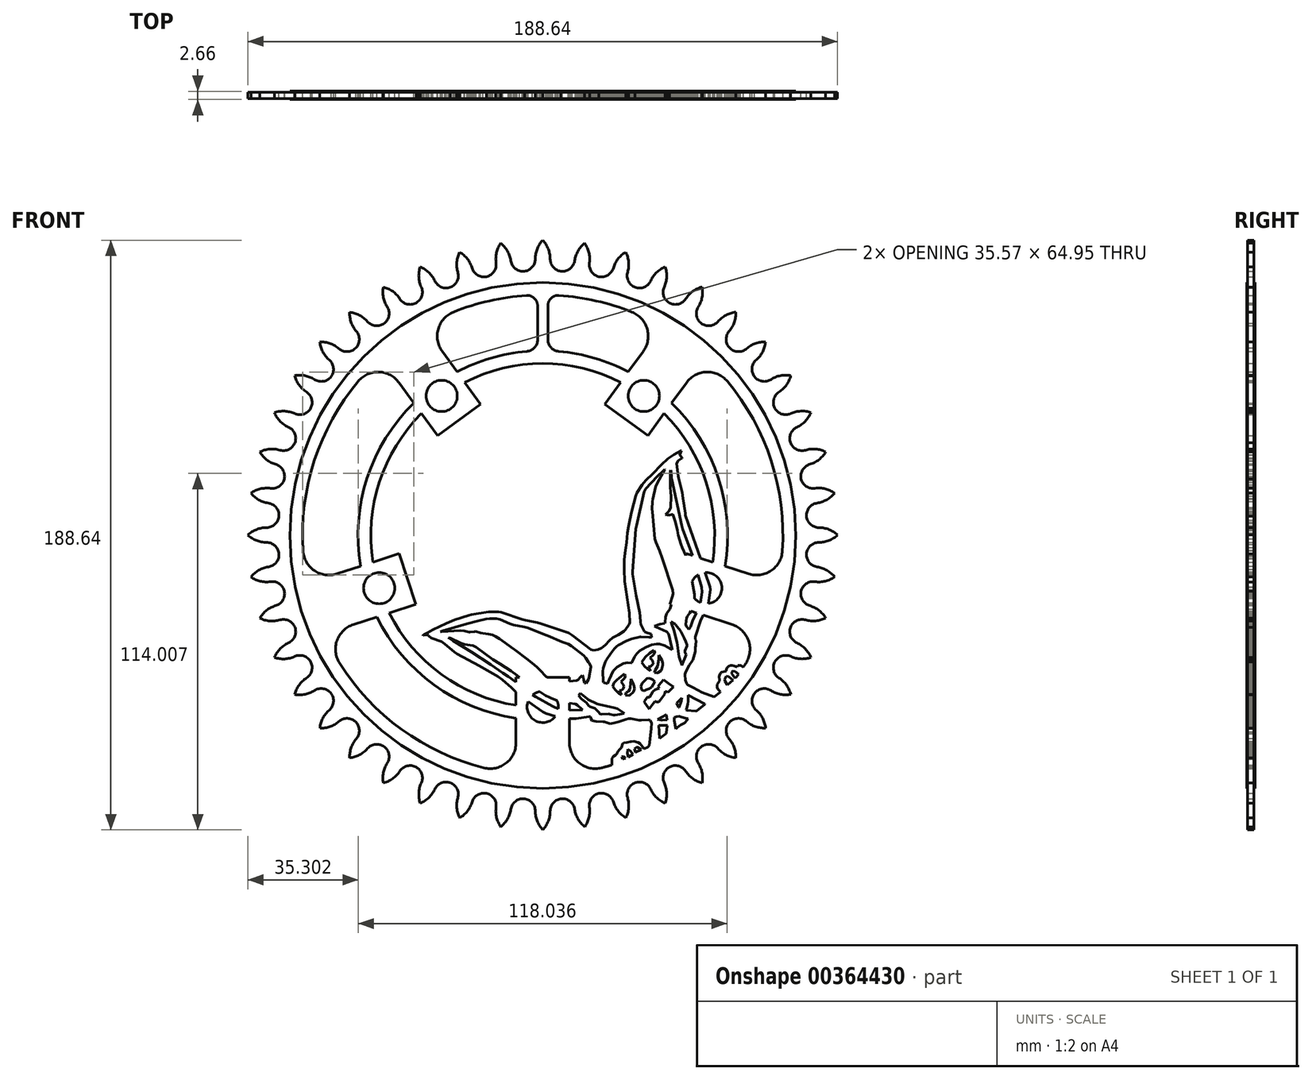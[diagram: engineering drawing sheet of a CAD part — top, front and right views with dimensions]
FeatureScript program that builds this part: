
annotation { "Feature Type Name" : "Feature", "Feature Type Description" : "" }
export const myFeature = defineFeature(function(context is Context, id is Id, definition is map)
    precondition{}
    {
        {
            var Q0;
            Q0=qCreatedBy(makeId("Front.planeOp"),FACE);
            var sketch = newSketch(context, id + "F0", { "sketchPlane" : qUnion([Q0])});
            skArc(sketch, "E0", {"start": v(-6.35, 84.36) * mm, "mid": v(-3.54, 85.52) * mm, "end": v(-2.38, 88.33) * mm});
            skArc(sketch, "E1.MirrorC", {"start": v(6.35, 84.36) * mm, "mid": v(3.54, 85.53) * mm, "end": v(2.38, 88.33) * mm});
            skPoint(sketch, "E2.orphan", {"position": v(12.57, 87.43) * mm});
            skPoint(sketch, "E3.trimOffspring.end.orphan", {"position": v(-12.57, 87.43) * mm});
            skLineSegment(sketch, "E4.trimOffspring", {"start": v(-5.78, 84.4) * mm, "end": v(-5.79, 84.4) * mm});
            skLineSegment(sketch, "E5.trimOffspring", {"start": v(5.78, 84.4) * mm, "end": v(5.79, 84.4) * mm});
            skPoint(sketch, "E6.MirrorCS.start.orphan", {"position": v(6.35, 0) * mm});
            skPoint(sketch, "E7.start.orphan", {"position": v(-6.35, 0) * mm});
            skArc(sketch, "E8.trimOffspring", {"start": v(-2.38, 88.33) * mm, "mid": v(-1.77, 91.55) * mm, "end": v(-0.01, 94.32) * mm});
            skPoint(sketch, "E9.trimOffspring.end.orphan", {"position": v(0, 88.33) * mm});
            skArc(sketch, "E10.trimOffspring", {"start": v(2.38, 88.33) * mm, "mid": v(1.76, 91.56) * mm, "end": v(-0.01, 94.32) * mm});
            skArc(sketch, "E11.1.0", {"start": v(-10.21, 87.77) * mm, "mid": v(-11.3, 90.88) * mm, "end": v(-13.44, 93.36) * mm});
            skPoint(sketch, "E11.1.2", {"position": v(-18.86, 86.53) * mm});
            skPoint(sketch, "E11.1.3", {"position": v(-6.29, 88.34) * mm});
            skArc(sketch, "E11.1.4", {"start": v(-14.93, 87.1) * mm, "mid": v(-14.78, 90.37) * mm, "end": v(-13.44, 93.36) * mm});
            skArc(sketch, "E11.1.5", {"start": v(-5.72, 84.4) * mm, "mid": v(-8.67, 85.16) * mm, "end": v(-10.21, 87.77) * mm});
            skArc(sketch, "E11.1.6", {"start": v(-18.3, 82.6) * mm, "mid": v(-15.68, 84.15) * mm, "end": v(-14.93, 87.1) * mm});
            skArc(sketch, "E11.2.0", {"start": v(-22.6, 85.43) * mm, "mid": v(-24.1, 88.34) * mm, "end": v(-26.59, 90.5) * mm});
            skPoint(sketch, "E11.2.1", {"position": v(-24.88, 84.75) * mm});
            skPoint(sketch, "E11.2.2", {"position": v(-30.98, 82.96) * mm});
            skPoint(sketch, "E11.2.3", {"position": v(-18.8, 86.54) * mm});
            skArc(sketch, "E11.2.4", {"start": v(-27.17, 84.08) * mm, "mid": v(-27.5, 87.35) * mm, "end": v(-26.59, 90.5) * mm});
            skArc(sketch, "E11.2.5", {"start": v(-17.67, 82.73) * mm, "mid": v(-20.7, 83.06) * mm, "end": v(-22.6, 85.43) * mm});
            skArc(sketch, "E11.2.6", {"start": v(-29.86, 79.16) * mm, "mid": v(-27.5, 81.06) * mm, "end": v(-27.17, 84.08) * mm});
            skArc(sketch, "E11.3.0", {"start": v(-34.53, 81.34) * mm, "mid": v(-36.43, 84.01) * mm, "end": v(-39.2, 85.8) * mm});
            skPoint(sketch, "E11.3.1", {"position": v(-36.7, 80.35) * mm});
            skPoint(sketch, "E11.3.2", {"position": v(-42.47, 77.71) * mm});
            skPoint(sketch, "E11.3.3", {"position": v(-30.92, 82.99) * mm});
            skArc(sketch, "E11.3.4", {"start": v(-38.86, 79.36) * mm, "mid": v(-39.64, 82.54) * mm, "end": v(-39.2, 85.8) * mm});
            skArc(sketch, "E11.3.5", {"start": v(-29.27, 79.38) * mm, "mid": v(-32.3, 79.27) * mm, "end": v(-34.53, 81.34) * mm});
            skArc(sketch, "E11.3.6", {"start": v(-40.82, 74.1) * mm, "mid": v(-38.75, 76.32) * mm, "end": v(-38.86, 79.36) * mm});
            skArc(sketch, "E11.4.0", {"start": v(-45.75, 75.6) * mm, "mid": v(-48.02, 77.97) * mm, "end": v(-51, 79.34) * mm});
            skPoint(sketch, "E11.4.1", {"position": v(-47.75, 74.3) * mm});
            skPoint(sketch, "E11.4.2", {"position": v(-53.1, 70.88) * mm});
            skPoint(sketch, "E11.4.3", {"position": v(-42.41, 77.74) * mm});
            skArc(sketch, "E11.4.4", {"start": v(-49.76, 73.02) * mm, "mid": v(-50.98, 76.06) * mm, "end": v(-51, 79.34) * mm});
            skArc(sketch, "E11.4.5", {"start": v(-40.27, 74.4) * mm, "mid": v(-43.26, 73.86) * mm, "end": v(-45.75, 75.6) * mm});
            skArc(sketch, "E11.4.6", {"start": v(-50.95, 67.54) * mm, "mid": v(-49.22, 70.03) * mm, "end": v(-49.76, 73.02) * mm});
            skArc(sketch, "E11.5.0", {"start": v(-56.05, 68.32) * mm, "mid": v(-58.63, 70.35) * mm, "end": v(-61.78, 71.28) * mm});
            skPoint(sketch, "E11.5.1", {"position": v(-57.84, 66.76) * mm});
            skPoint(sketch, "E11.5.2", {"position": v(-62.64, 62.6) * mm});
            skPoint(sketch, "E11.5.3", {"position": v(-53.04, 70.91) * mm});
            skArc(sketch, "E11.5.4", {"start": v(-59.64, 65.2) * mm, "mid": v(-61.29, 68.03) * mm, "end": v(-61.78, 71.28) * mm});
            skArc(sketch, "E11.5.5", {"start": v(-50.44, 67.92) * mm, "mid": v(-53.33, 66.96) * mm, "end": v(-56.05, 68.32) * mm});
            skArc(sketch, "E11.5.6", {"start": v(-60.04, 59.6) * mm, "mid": v(-58.68, 62.32) * mm, "end": v(-59.64, 65.2) * mm});
            skArc(sketch, "E11.6.0", {"start": v(-65.2, 59.65) * mm, "mid": v(-68.04, 61.29) * mm, "end": v(-71.3, 61.76) * mm});
            skPoint(sketch, "E11.6.1", {"position": v(-66.75, 57.85) * mm});
            skPoint(sketch, "E11.6.2", {"position": v(-70.91, 53.05) * mm});
            skPoint(sketch, "E11.6.3", {"position": v(-62.6, 62.64) * mm});
            skArc(sketch, "E11.6.4", {"start": v(-68.31, 56.05) * mm, "mid": v(-70.35, 58.62) * mm, "end": v(-71.3, 61.76) * mm});
            skArc(sketch, "E11.6.5", {"start": v(-59.6, 60.05) * mm, "mid": v(-62.31, 58.69) * mm, "end": v(-65.2, 59.65) * mm});
            skArc(sketch, "E11.6.6", {"start": v(-67.91, 50.45) * mm, "mid": v(-66.95, 53.33) * mm, "end": v(-68.31, 56.05) * mm});
            skArc(sketch, "E11.7.0", {"start": v(-73.02, 49.76) * mm, "mid": v(-76.07, 50.98) * mm, "end": v(-79.35, 50.99) * mm});
            skPoint(sketch, "E11.7.1", {"position": v(-74.3, 47.76) * mm});
            skPoint(sketch, "E11.7.2", {"position": v(-77.74, 42.42) * mm});
            skPoint(sketch, "E11.7.3", {"position": v(-70.87, 53.1) * mm});
            skArc(sketch, "E11.7.4", {"start": v(-75.6, 45.75) * mm, "mid": v(-77.97, 48.01) * mm, "end": v(-79.35, 50.99) * mm});
            skArc(sketch, "E11.7.5", {"start": v(-67.53, 50.95) * mm, "mid": v(-70.03, 49.22) * mm, "end": v(-73.02, 49.76) * mm});
            skArc(sketch, "E11.7.6", {"start": v(-74.4, 40.27) * mm, "mid": v(-73.86, 43.26) * mm, "end": v(-75.6, 45.75) * mm});
            skArc(sketch, "E11.8.0", {"start": v(-79.36, 38.86) * mm, "mid": v(-82.55, 39.63) * mm, "end": v(-85.8, 39.17) * mm});
            skPoint(sketch, "E11.8.1", {"position": v(-80.34, 36.7) * mm});
            skPoint(sketch, "E11.8.2", {"position": v(-82.98, 30.92) * mm});
            skPoint(sketch, "E11.8.3", {"position": v(-77.7, 42.47) * mm});
            skArc(sketch, "E11.8.4", {"start": v(-81.33, 34.53) * mm, "mid": v(-84.01, 36.42) * mm, "end": v(-85.8, 39.17) * mm});
            skArc(sketch, "E11.8.5", {"start": v(-74.1, 40.82) * mm, "mid": v(-76.32, 38.75) * mm, "end": v(-79.36, 38.86) * mm});
            skArc(sketch, "E11.8.6", {"start": v(-79.37, 29.27) * mm, "mid": v(-79.26, 32.3) * mm, "end": v(-81.33, 34.53) * mm});
            skArc(sketch, "E11.9.0", {"start": v(-84.08, 27.17) * mm, "mid": v(-87.35, 27.48) * mm, "end": v(-90.5, 26.56) * mm});
            skPoint(sketch, "E11.9.1", {"position": v(-84.75, 24.89) * mm});
            skPoint(sketch, "E11.9.2", {"position": v(-86.54, 18.8) * mm});
            skPoint(sketch, "E11.9.3", {"position": v(-82.96, 30.98) * mm});
            skArc(sketch, "E11.9.4", {"start": v(-85.42, 22.6) * mm, "mid": v(-88.34, 24.1) * mm, "end": v(-90.5, 26.56) * mm});
            skArc(sketch, "E11.9.5", {"start": v(-79.15, 29.86) * mm, "mid": v(-81.06, 27.5) * mm, "end": v(-84.08, 27.17) * mm});
            skArc(sketch, "E11.9.6", {"start": v(-82.73, 17.68) * mm, "mid": v(-83.05, 20.7) * mm, "end": v(-85.42, 22.6) * mm});
            skArc(sketch, "E11.10.0", {"start": v(-87.1, 14.93) * mm, "mid": v(-90.37, 14.77) * mm, "end": v(-93.36, 13.41) * mm});
            skPoint(sketch, "E11.10.1", {"position": v(-87.43, 12.57) * mm});
            skPoint(sketch, "E11.10.2", {"position": v(-88.33, 6.29) * mm});
            skPoint(sketch, "E11.10.3", {"position": v(-86.52, 18.86) * mm});
            skArc(sketch, "E11.10.4", {"start": v(-87.77, 10.22) * mm, "mid": v(-90.87, 11.28) * mm, "end": v(-93.36, 13.41) * mm});
            skArc(sketch, "E11.10.5", {"start": v(-82.6, 18.3) * mm, "mid": v(-84.15, 15.68) * mm, "end": v(-87.1, 14.93) * mm});
            skArc(sketch, "E11.10.6", {"start": v(-84.4, 5.72) * mm, "mid": v(-85.15, 8.67) * mm, "end": v(-87.77, 10.22) * mm});
            skArc(sketch, "E11.11.0", {"start": v(-88.33, 2.38) * mm, "mid": v(-91.55, 1.76) * mm, "end": v(-94.32, 0) * mm});
            skPoint(sketch, "E11.11.1", {"position": v(-88.33, 0) * mm});
            skPoint(sketch, "E11.11.2", {"position": v(-88.33, -6.35) * mm});
            skPoint(sketch, "E11.11.3", {"position": v(-88.33, 6.35) * mm});
            skArc(sketch, "E11.11.4", {"start": v(-88.33, -2.38) * mm, "mid": v(-91.55, -1.77) * mm, "end": v(-94.32, 0) * mm});
            skArc(sketch, "E11.11.5", {"start": v(-84.36, 6.35) * mm, "mid": v(-85.52, 3.55) * mm, "end": v(-88.33, 2.38) * mm});
            skArc(sketch, "E11.11.6", {"start": v(-84.36, -6.35) * mm, "mid": v(-85.52, -3.54) * mm, "end": v(-88.33, -2.38) * mm});
            skArc(sketch, "E11.12.0", {"start": v(-87.77, -10.21) * mm, "mid": v(-90.87, -11.29) * mm, "end": v(-93.36, -13.43) * mm});
            skPoint(sketch, "E11.12.1", {"position": v(-87.43, -12.57) * mm});
            skPoint(sketch, "E11.12.2", {"position": v(-86.52, -18.85) * mm});
            skPoint(sketch, "E11.12.3", {"position": v(-88.33, -6.28) * mm});
            skArc(sketch, "E11.12.4", {"start": v(-87.09, -14.92) * mm, "mid": v(-90.37, -14.78) * mm, "end": v(-93.36, -13.43) * mm});
            skArc(sketch, "E11.12.5", {"start": v(-84.4, -5.72) * mm, "mid": v(-85.16, -8.66) * mm, "end": v(-87.77, -10.21) * mm});
            skArc(sketch, "E11.12.6", {"start": v(-82.6, -18.29) * mm, "mid": v(-84.15, -15.67) * mm, "end": v(-87.09, -14.92) * mm});
            skArc(sketch, "E11.13.0", {"start": v(-85.42, -22.6) * mm, "mid": v(-88.34, -24.1) * mm, "end": v(-90.5, -26.58) * mm});
            skPoint(sketch, "E11.13.1", {"position": v(-84.75, -24.88) * mm});
            skPoint(sketch, "E11.13.2", {"position": v(-82.96, -30.97) * mm});
            skPoint(sketch, "E11.13.3", {"position": v(-86.54, -18.79) * mm});
            skArc(sketch, "E11.13.4", {"start": v(-84.08, -27.16) * mm, "mid": v(-87.34, -27.49) * mm, "end": v(-90.5, -26.58) * mm});
            skArc(sketch, "E11.13.5", {"start": v(-82.73, -17.67) * mm, "mid": v(-83.06, -20.7) * mm, "end": v(-85.42, -22.6) * mm});
            skArc(sketch, "E11.13.6", {"start": v(-79.15, -29.85) * mm, "mid": v(-81.06, -27.49) * mm, "end": v(-84.08, -27.16) * mm});
            skArc(sketch, "E11.14.0", {"start": v(-81.34, -34.52) * mm, "mid": v(-84.01, -36.43) * mm, "end": v(-85.8, -39.2) * mm});
            skPoint(sketch, "E11.14.1", {"position": v(-80.34, -36.69) * mm});
            skPoint(sketch, "E11.14.2", {"position": v(-77.7, -42.46) * mm});
            skPoint(sketch, "E11.14.3", {"position": v(-82.98, -30.91) * mm});
            skArc(sketch, "E11.14.4", {"start": v(-79.36, -38.85) * mm, "mid": v(-82.54, -39.64) * mm, "end": v(-85.8, -39.2) * mm});
            skArc(sketch, "E11.14.5", {"start": v(-79.37, -29.26) * mm, "mid": v(-79.26, -32.3) * mm, "end": v(-81.34, -34.52) * mm});
            skArc(sketch, "E11.14.6", {"start": v(-74.1, -40.82) * mm, "mid": v(-76.32, -38.75) * mm, "end": v(-79.36, -38.85) * mm});
            skArc(sketch, "E11.15.0", {"start": v(-75.6, -45.75) * mm, "mid": v(-77.97, -48.02) * mm, "end": v(-79.34, -51) * mm});
            skPoint(sketch, "E11.15.1", {"position": v(-74.3, -47.75) * mm});
            skPoint(sketch, "E11.15.2", {"position": v(-70.87, -53.1) * mm});
            skPoint(sketch, "E11.15.3", {"position": v(-77.74, -42.4) * mm});
            skArc(sketch, "E11.15.4", {"start": v(-73.02, -49.75) * mm, "mid": v(-76.06, -50.98) * mm, "end": v(-79.34, -51) * mm});
            skArc(sketch, "E11.15.5", {"start": v(-74.4, -40.26) * mm, "mid": v(-73.86, -43.25) * mm, "end": v(-75.6, -45.75) * mm});
            skArc(sketch, "E11.15.6", {"start": v(-67.53, -50.94) * mm, "mid": v(-70.03, -49.21) * mm, "end": v(-73.02, -49.75) * mm});
            skArc(sketch, "E11.16.0", {"start": v(-68.31, -56.04) * mm, "mid": v(-70.34, -58.62) * mm, "end": v(-71.27, -61.77) * mm});
            skPoint(sketch, "E11.16.1", {"position": v(-66.75, -57.84) * mm});
            skPoint(sketch, "E11.16.2", {"position": v(-62.6, -62.64) * mm});
            skPoint(sketch, "E11.16.3", {"position": v(-70.91, -53.04) * mm});
            skArc(sketch, "E11.16.4", {"start": v(-65.2, -59.64) * mm, "mid": v(-68.03, -61.29) * mm, "end": v(-71.27, -61.77) * mm});
            skArc(sketch, "E11.16.5", {"start": v(-67.91, -50.44) * mm, "mid": v(-66.95, -53.32) * mm, "end": v(-68.31, -56.04) * mm});
            skArc(sketch, "E11.16.6", {"start": v(-59.6, -60.04) * mm, "mid": v(-62.31, -58.68) * mm, "end": v(-65.2, -59.64) * mm});
            skArc(sketch, "E11.17.0", {"start": v(-59.64, -65.2) * mm, "mid": v(-61.28, -68.04) * mm, "end": v(-61.76, -71.29) * mm});
            skPoint(sketch, "E11.17.1", {"position": v(-57.84, -66.75) * mm});
            skPoint(sketch, "E11.17.2", {"position": v(-53.04, -70.9) * mm});
            skPoint(sketch, "E11.17.3", {"position": v(-62.64, -62.6) * mm});
            skArc(sketch, "E11.17.4", {"start": v(-56.04, -68.3) * mm, "mid": v(-58.61, -70.34) * mm, "end": v(-61.76, -71.29) * mm});
            skArc(sketch, "E11.17.5", {"start": v(-60.04, -59.6) * mm, "mid": v(-58.68, -62.3) * mm, "end": v(-59.64, -65.2) * mm});
            skArc(sketch, "E11.17.6", {"start": v(-50.44, -67.9) * mm, "mid": v(-53.33, -66.95) * mm, "end": v(-56.04, -68.3) * mm});
            skArc(sketch, "E11.18.0", {"start": v(-49.76, -73.02) * mm, "mid": v(-50.98, -76.07) * mm, "end": v(-50.98, -79.35) * mm});
            skPoint(sketch, "E11.18.1", {"position": v(-47.75, -74.3) * mm});
            skPoint(sketch, "E11.18.2", {"position": v(-42.41, -77.73) * mm});
            skPoint(sketch, "E11.18.3", {"position": v(-53.1, -70.87) * mm});
            skArc(sketch, "E11.18.4", {"start": v(-45.75, -75.59) * mm, "mid": v(-48, -77.97) * mm, "end": v(-50.98, -79.35) * mm});
            skArc(sketch, "E11.18.5", {"start": v(-50.95, -67.53) * mm, "mid": v(-49.22, -70.03) * mm, "end": v(-49.76, -73.02) * mm});
            skArc(sketch, "E11.18.6", {"start": v(-40.27, -74.4) * mm, "mid": v(-43.26, -73.86) * mm, "end": v(-45.75, -75.59) * mm});
            skArc(sketch, "E11.19.0", {"start": v(-38.86, -79.36) * mm, "mid": v(-39.63, -82.55) * mm, "end": v(-39.17, -85.8) * mm});
            skPoint(sketch, "E11.19.1", {"position": v(-36.7, -80.34) * mm});
            skPoint(sketch, "E11.19.2", {"position": v(-30.92, -82.98) * mm});
            skPoint(sketch, "E11.19.3", {"position": v(-42.47, -77.7) * mm});
            skArc(sketch, "E11.19.4", {"start": v(-34.53, -81.33) * mm, "mid": v(-36.42, -84) * mm, "end": v(-39.17, -85.8) * mm});
            skArc(sketch, "E11.19.5", {"start": v(-40.82, -74.1) * mm, "mid": v(-38.75, -76.32) * mm, "end": v(-38.86, -79.36) * mm});
            skArc(sketch, "E11.19.6", {"start": v(-29.27, -79.37) * mm, "mid": v(-32.3, -79.26) * mm, "end": v(-34.53, -81.33) * mm});
            skArc(sketch, "E11.20.0", {"start": v(-27.17, -84.08) * mm, "mid": v(-27.48, -87.35) * mm, "end": v(-26.56, -90.5) * mm});
            skPoint(sketch, "E11.20.1", {"position": v(-24.88, -84.74) * mm});
            skPoint(sketch, "E11.20.2", {"position": v(-18.8, -86.53) * mm});
            skPoint(sketch, "E11.20.3", {"position": v(-30.98, -82.96) * mm});
            skArc(sketch, "E11.20.4", {"start": v(-22.6, -85.42) * mm, "mid": v(-24.1, -88.34) * mm, "end": v(-26.56, -90.5) * mm});
            skArc(sketch, "E11.20.5", {"start": v(-29.86, -79.15) * mm, "mid": v(-27.5, -81.06) * mm, "end": v(-27.17, -84.08) * mm});
            skArc(sketch, "E11.20.6", {"start": v(-17.67, -82.73) * mm, "mid": v(-20.7, -83.05) * mm, "end": v(-22.6, -85.42) * mm});
            skArc(sketch, "E11.21.0", {"start": v(-14.93, -87.09) * mm, "mid": v(-14.77, -90.37) * mm, "end": v(-13.4, -93.36) * mm});
            skPoint(sketch, "E11.21.1", {"position": v(-12.57, -87.42) * mm});
            skPoint(sketch, "E11.21.2", {"position": v(-6.29, -88.33) * mm});
            skPoint(sketch, "E11.21.3", {"position": v(-18.86, -86.52) * mm});
            skArc(sketch, "E11.21.4", {"start": v(-10.21, -87.76) * mm, "mid": v(-11.28, -90.87) * mm, "end": v(-13.4, -93.36) * mm});
            skArc(sketch, "E11.21.5", {"start": v(-18.3, -82.6) * mm, "mid": v(-15.68, -84.14) * mm, "end": v(-14.93, -87.09) * mm});
            skArc(sketch, "E11.21.6", {"start": v(-5.72, -84.4) * mm, "mid": v(-8.66, -85.15) * mm, "end": v(-10.21, -87.76) * mm});
            skArc(sketch, "E11.22.0", {"start": v(-2.38, -88.33) * mm, "mid": v(-1.76, -91.55) * mm, "end": v(0.01, -94.32) * mm});
            skPoint(sketch, "E11.22.1", {"position": v(0, -88.32) * mm});
            skPoint(sketch, "E11.22.2", {"position": v(6.35, -88.32) * mm});
            skPoint(sketch, "E11.22.3", {"position": v(-6.35, -88.32) * mm});
            skArc(sketch, "E11.22.4", {"start": v(2.38, -88.32) * mm, "mid": v(1.77, -91.55) * mm, "end": v(0.01, -94.32) * mm});
            skArc(sketch, "E11.22.5", {"start": v(-6.35, -84.35) * mm, "mid": v(-3.54, -85.52) * mm, "end": v(-2.38, -88.33) * mm});
            skArc(sketch, "E11.22.6", {"start": v(6.35, -84.35) * mm, "mid": v(3.54, -85.52) * mm, "end": v(2.38, -88.32) * mm});
            skArc(sketch, "E11.23.0", {"start": v(10.21, -87.77) * mm, "mid": v(11.3, -90.87) * mm, "end": v(13.44, -93.35) * mm});
            skPoint(sketch, "E11.23.1", {"position": v(12.57, -87.42) * mm});
            skPoint(sketch, "E11.23.2", {"position": v(18.86, -86.52) * mm});
            skPoint(sketch, "E11.23.3", {"position": v(6.29, -88.33) * mm});
            skArc(sketch, "E11.23.4", {"start": v(14.93, -87.08) * mm, "mid": v(14.78, -90.36) * mm, "end": v(13.44, -93.35) * mm});
            skArc(sketch, "E11.23.5", {"start": v(5.72, -84.4) * mm, "mid": v(8.67, -85.15) * mm, "end": v(10.21, -87.77) * mm});
            skArc(sketch, "E11.23.6", {"start": v(18.3, -82.6) * mm, "mid": v(15.68, -84.14) * mm, "end": v(14.93, -87.08) * mm});
            skArc(sketch, "E11.24.0", {"start": v(22.6, -85.42) * mm, "mid": v(24.1, -88.34) * mm, "end": v(26.59, -90.5) * mm});
            skPoint(sketch, "E11.24.1", {"position": v(24.88, -84.74) * mm});
            skPoint(sketch, "E11.24.2", {"position": v(30.98, -82.96) * mm});
            skPoint(sketch, "E11.24.3", {"position": v(18.8, -86.53) * mm});
            skArc(sketch, "E11.24.4", {"start": v(27.17, -84.07) * mm, "mid": v(27.5, -87.34) * mm, "end": v(26.59, -90.5) * mm});
            skArc(sketch, "E11.24.5", {"start": v(17.67, -82.73) * mm, "mid": v(20.7, -83.05) * mm, "end": v(22.6, -85.42) * mm});
            skArc(sketch, "E11.24.6", {"start": v(29.86, -79.15) * mm, "mid": v(27.5, -81.05) * mm, "end": v(27.17, -84.07) * mm});
            skArc(sketch, "E11.25.0", {"start": v(34.53, -81.33) * mm, "mid": v(36.43, -84) * mm, "end": v(39.2, -85.79) * mm});
            skPoint(sketch, "E11.25.1", {"position": v(36.7, -80.34) * mm});
            skPoint(sketch, "E11.25.2", {"position": v(42.47, -77.7) * mm});
            skPoint(sketch, "E11.25.3", {"position": v(30.92, -82.98) * mm});
            skArc(sketch, "E11.25.4", {"start": v(38.86, -79.35) * mm, "mid": v(39.64, -82.54) * mm, "end": v(39.2, -85.79) * mm});
            skArc(sketch, "E11.25.5", {"start": v(29.27, -79.37) * mm, "mid": v(32.3, -79.26) * mm, "end": v(34.53, -81.33) * mm});
            skArc(sketch, "E11.25.6", {"start": v(40.82, -74.1) * mm, "mid": v(38.75, -76.32) * mm, "end": v(38.86, -79.35) * mm});
            skArc(sketch, "E11.26.0", {"start": v(45.75, -75.6) * mm, "mid": v(48.02, -77.97) * mm, "end": v(51, -79.34) * mm});
            skPoint(sketch, "E11.26.1", {"position": v(47.75, -74.3) * mm});
            skPoint(sketch, "E11.26.2", {"position": v(53.1, -70.87) * mm});
            skPoint(sketch, "E11.26.3", {"position": v(42.41, -77.73) * mm});
            skArc(sketch, "E11.26.4", {"start": v(49.76, -73.01) * mm, "mid": v(50.98, -76.06) * mm, "end": v(51, -79.34) * mm});
            skArc(sketch, "E11.26.5", {"start": v(40.27, -74.4) * mm, "mid": v(43.26, -73.86) * mm, "end": v(45.75, -75.6) * mm});
            skArc(sketch, "E11.26.6", {"start": v(50.95, -67.53) * mm, "mid": v(49.22, -70.02) * mm, "end": v(49.76, -73.01) * mm});
            skArc(sketch, "E11.27.0", {"start": v(56.05, -68.31) * mm, "mid": v(58.63, -70.34) * mm, "end": v(61.78, -71.27) * mm});
            skPoint(sketch, "E11.27.1", {"position": v(57.84, -66.75) * mm});
            skPoint(sketch, "E11.27.2", {"position": v(62.64, -62.6) * mm});
            skPoint(sketch, "E11.27.3", {"position": v(53.04, -70.9) * mm});
            skArc(sketch, "E11.27.4", {"start": v(59.64, -65.19) * mm, "mid": v(61.29, -68.03) * mm, "end": v(61.78, -71.27) * mm});
            skArc(sketch, "E11.27.5", {"start": v(50.44, -67.9) * mm, "mid": v(53.33, -66.95) * mm, "end": v(56.05, -68.31) * mm});
            skArc(sketch, "E11.27.6", {"start": v(60.04, -59.6) * mm, "mid": v(58.68, -62.3) * mm, "end": v(59.64, -65.19) * mm});
            skArc(sketch, "E11.28.0", {"start": v(65.2, -59.64) * mm, "mid": v(68.04, -61.28) * mm, "end": v(71.3, -61.75) * mm});
            skPoint(sketch, "E11.28.1", {"position": v(66.75, -57.84) * mm});
            skPoint(sketch, "E11.28.2", {"position": v(70.91, -53.04) * mm});
            skPoint(sketch, "E11.28.3", {"position": v(62.6, -62.64) * mm});
            skArc(sketch, "E11.28.4", {"start": v(68.31, -56.04) * mm, "mid": v(70.35, -58.61) * mm, "end": v(71.3, -61.75) * mm});
            skArc(sketch, "E11.28.5", {"start": v(59.6, -60.04) * mm, "mid": v(62.31, -58.68) * mm, "end": v(65.2, -59.64) * mm});
            skArc(sketch, "E11.28.6", {"start": v(67.91, -50.44) * mm, "mid": v(66.95, -53.32) * mm, "end": v(68.31, -56.04) * mm});
            skArc(sketch, "E11.29.0", {"start": v(73.02, -49.75) * mm, "mid": v(76.07, -50.97) * mm, "end": v(79.35, -50.98) * mm});
            skPoint(sketch, "E11.29.1", {"position": v(74.3, -47.75) * mm});
            skPoint(sketch, "E11.29.2", {"position": v(77.74, -42.4) * mm});
            skPoint(sketch, "E11.29.3", {"position": v(70.87, -53.1) * mm});
            skArc(sketch, "E11.29.4", {"start": v(75.6, -45.75) * mm, "mid": v(77.97, -48) * mm, "end": v(79.35, -50.98) * mm});
            skArc(sketch, "E11.29.5", {"start": v(67.53, -50.94) * mm, "mid": v(70.03, -49.21) * mm, "end": v(73.02, -49.75) * mm});
            skArc(sketch, "E11.29.6", {"start": v(74.4, -40.26) * mm, "mid": v(73.86, -43.25) * mm, "end": v(75.6, -45.75) * mm});
            skArc(sketch, "E11.30.0", {"start": v(79.36, -38.86) * mm, "mid": v(82.55, -39.63) * mm, "end": v(85.8, -39.17) * mm});
            skPoint(sketch, "E11.30.1", {"position": v(80.34, -36.69) * mm});
            skPoint(sketch, "E11.30.2", {"position": v(82.98, -30.91) * mm});
            skPoint(sketch, "E11.30.3", {"position": v(77.7, -42.46) * mm});
            skArc(sketch, "E11.30.4", {"start": v(81.33, -34.52) * mm, "mid": v(84.01, -36.42) * mm, "end": v(85.8, -39.17) * mm});
            skArc(sketch, "E11.30.5", {"start": v(74.1, -40.82) * mm, "mid": v(76.32, -38.74) * mm, "end": v(79.36, -38.86) * mm});
            skArc(sketch, "E11.30.6", {"start": v(79.37, -29.26) * mm, "mid": v(79.26, -32.3) * mm, "end": v(81.33, -34.52) * mm});
            skArc(sketch, "E11.31.0", {"start": v(84.08, -27.17) * mm, "mid": v(87.35, -27.48) * mm, "end": v(90.5, -26.56) * mm});
            skPoint(sketch, "E11.31.1", {"position": v(84.75, -24.88) * mm});
            skPoint(sketch, "E11.31.2", {"position": v(86.54, -18.79) * mm});
            skPoint(sketch, "E11.31.3", {"position": v(82.96, -30.97) * mm});
            skArc(sketch, "E11.31.4", {"start": v(85.42, -22.6) * mm, "mid": v(88.34, -24.1) * mm, "end": v(90.5, -26.56) * mm});
            skArc(sketch, "E11.31.5", {"start": v(79.15, -29.85) * mm, "mid": v(81.06, -27.49) * mm, "end": v(84.08, -27.17) * mm});
            skArc(sketch, "E11.31.6", {"start": v(82.73, -17.67) * mm, "mid": v(83.05, -20.7) * mm, "end": v(85.42, -22.6) * mm});
            skArc(sketch, "E11.32.0", {"start": v(87.1, -14.92) * mm, "mid": v(90.37, -14.76) * mm, "end": v(93.36, -13.4) * mm});
            skPoint(sketch, "E11.32.1", {"position": v(87.43, -12.57) * mm});
            skPoint(sketch, "E11.32.2", {"position": v(88.33, -6.28) * mm});
            skPoint(sketch, "E11.32.3", {"position": v(86.52, -18.85) * mm});
            skArc(sketch, "E11.32.4", {"start": v(87.77, -10.2) * mm, "mid": v(90.87, -11.27) * mm, "end": v(93.36, -13.4) * mm});
            skArc(sketch, "E11.32.5", {"start": v(82.6, -18.29) * mm, "mid": v(84.15, -15.67) * mm, "end": v(87.1, -14.92) * mm});
            skArc(sketch, "E11.32.6", {"start": v(84.4, -5.72) * mm, "mid": v(85.15, -8.66) * mm, "end": v(87.77, -10.2) * mm});
            skArc(sketch, "E11.33.0", {"start": v(88.33, -2.38) * mm, "mid": v(91.55, -1.75) * mm, "end": v(94.32, 0.02) * mm});
            skPoint(sketch, "E11.33.1", {"position": v(88.33, 0) * mm});
            skPoint(sketch, "E11.33.2", {"position": v(88.33, 6.35) * mm});
            skPoint(sketch, "E11.33.3", {"position": v(88.33, -6.35) * mm});
            skArc(sketch, "E11.33.4", {"start": v(88.33, 2.38) * mm, "mid": v(91.55, 1.77) * mm, "end": v(94.32, 0.02) * mm});
            skArc(sketch, "E11.33.5", {"start": v(84.36, -6.35) * mm, "mid": v(85.52, -3.54) * mm, "end": v(88.33, -2.38) * mm});
            skArc(sketch, "E11.33.6", {"start": v(84.36, 6.35) * mm, "mid": v(85.52, 3.55) * mm, "end": v(88.33, 2.38) * mm});
            skArc(sketch, "E11.34.0", {"start": v(87.77, 10.22) * mm, "mid": v(90.87, 11.3) * mm, "end": v(93.36, 13.44) * mm});
            skPoint(sketch, "E11.34.1", {"position": v(87.43, 12.57) * mm});
            skPoint(sketch, "E11.34.2", {"position": v(86.52, 18.86) * mm});
            skPoint(sketch, "E11.34.3", {"position": v(88.33, 6.29) * mm});
            skArc(sketch, "E11.34.4", {"start": v(87.09, 14.93) * mm, "mid": v(90.37, 14.78) * mm, "end": v(93.36, 13.44) * mm});
            skArc(sketch, "E11.34.5", {"start": v(84.4, 5.72) * mm, "mid": v(85.16, 8.67) * mm, "end": v(87.77, 10.22) * mm});
            skArc(sketch, "E11.34.6", {"start": v(82.6, 18.3) * mm, "mid": v(84.15, 15.68) * mm, "end": v(87.09, 14.93) * mm});
            skArc(sketch, "E11.35.0", {"start": v(85.42, 22.6) * mm, "mid": v(88.34, 24.11) * mm, "end": v(90.5, 26.59) * mm});
            skPoint(sketch, "E11.35.1", {"position": v(84.75, 24.89) * mm});
            skPoint(sketch, "E11.35.2", {"position": v(82.96, 30.98) * mm});
            skPoint(sketch, "E11.35.3", {"position": v(86.54, 18.8) * mm});
            skArc(sketch, "E11.35.4", {"start": v(84.08, 27.17) * mm, "mid": v(87.34, 27.5) * mm, "end": v(90.5, 26.59) * mm});
            skArc(sketch, "E11.35.5", {"start": v(82.73, 17.68) * mm, "mid": v(83.06, 20.7) * mm, "end": v(85.42, 22.6) * mm});
            skArc(sketch, "E11.35.6", {"start": v(79.15, 29.86) * mm, "mid": v(81.06, 27.5) * mm, "end": v(84.08, 27.17) * mm});
            skArc(sketch, "E11.36.0", {"start": v(81.34, 34.53) * mm, "mid": v(84.01, 36.44) * mm, "end": v(85.8, 39.2) * mm});
            skPoint(sketch, "E11.36.1", {"position": v(80.34, 36.7) * mm});
            skPoint(sketch, "E11.36.2", {"position": v(77.7, 42.47) * mm});
            skPoint(sketch, "E11.36.3", {"position": v(82.98, 30.92) * mm});
            skArc(sketch, "E11.36.4", {"start": v(79.36, 38.86) * mm, "mid": v(82.54, 39.64) * mm, "end": v(85.8, 39.2) * mm});
            skArc(sketch, "E11.36.5", {"start": v(79.37, 29.27) * mm, "mid": v(79.26, 32.3) * mm, "end": v(81.34, 34.53) * mm});
            skArc(sketch, "E11.36.6", {"start": v(74.1, 40.82) * mm, "mid": v(76.32, 38.75) * mm, "end": v(79.36, 38.86) * mm});
            skArc(sketch, "E11.37.0", {"start": v(75.6, 45.76) * mm, "mid": v(77.97, 48.02) * mm, "end": v(79.34, 51) * mm});
            skPoint(sketch, "E11.37.1", {"position": v(74.3, 47.76) * mm});
            skPoint(sketch, "E11.37.2", {"position": v(70.87, 53.1) * mm});
            skPoint(sketch, "E11.37.3", {"position": v(77.74, 42.42) * mm});
            skArc(sketch, "E11.37.4", {"start": v(73.02, 49.76) * mm, "mid": v(76.06, 50.99) * mm, "end": v(79.34, 51) * mm});
            skArc(sketch, "E11.37.5", {"start": v(74.4, 40.27) * mm, "mid": v(73.86, 43.26) * mm, "end": v(75.6, 45.76) * mm});
            skArc(sketch, "E11.37.6", {"start": v(67.53, 50.95) * mm, "mid": v(70.03, 49.22) * mm, "end": v(73.02, 49.76) * mm});
            skArc(sketch, "E11.38.0", {"start": v(68.31, 56.05) * mm, "mid": v(70.34, 58.63) * mm, "end": v(71.27, 61.78) * mm});
            skPoint(sketch, "E11.38.1", {"position": v(66.75, 57.85) * mm});
            skPoint(sketch, "E11.38.2", {"position": v(62.6, 62.64) * mm});
            skPoint(sketch, "E11.38.3", {"position": v(70.91, 53.05) * mm});
            skArc(sketch, "E11.38.4", {"start": v(65.2, 59.64) * mm, "mid": v(68.03, 61.3) * mm, "end": v(71.27, 61.78) * mm});
            skArc(sketch, "E11.38.5", {"start": v(67.91, 50.45) * mm, "mid": v(66.95, 53.33) * mm, "end": v(68.31, 56.05) * mm});
            skArc(sketch, "E11.38.6", {"start": v(59.6, 60.05) * mm, "mid": v(62.31, 58.69) * mm, "end": v(65.2, 59.64) * mm});
            skArc(sketch, "E11.39.0", {"start": v(59.64, 65.2) * mm, "mid": v(61.28, 68.05) * mm, "end": v(61.76, 71.3) * mm});
            skPoint(sketch, "E11.39.1", {"position": v(57.84, 66.76) * mm});
            skPoint(sketch, "E11.39.2", {"position": v(53.04, 70.91) * mm});
            skPoint(sketch, "E11.39.3", {"position": v(62.64, 62.6) * mm});
            skArc(sketch, "E11.39.4", {"start": v(56.04, 68.32) * mm, "mid": v(58.61, 70.35) * mm, "end": v(61.76, 71.3) * mm});
            skArc(sketch, "E11.39.5", {"start": v(60.04, 59.6) * mm, "mid": v(58.68, 62.32) * mm, "end": v(59.64, 65.2) * mm});
            skArc(sketch, "E11.39.6", {"start": v(50.44, 67.92) * mm, "mid": v(53.33, 66.96) * mm, "end": v(56.04, 68.32) * mm});
            skArc(sketch, "E11.40.0", {"start": v(49.76, 73.03) * mm, "mid": v(50.98, 76.07) * mm, "end": v(50.98, 79.36) * mm});
            skPoint(sketch, "E11.40.1", {"position": v(47.75, 74.3) * mm});
            skPoint(sketch, "E11.40.2", {"position": v(42.41, 77.74) * mm});
            skPoint(sketch, "E11.40.3", {"position": v(53.1, 70.88) * mm});
            skArc(sketch, "E11.40.4", {"start": v(45.75, 75.6) * mm, "mid": v(48, 77.98) * mm, "end": v(50.98, 79.36) * mm});
            skArc(sketch, "E11.40.5", {"start": v(50.95, 67.54) * mm, "mid": v(49.22, 70.03) * mm, "end": v(49.76, 73.03) * mm});
            skArc(sketch, "E11.40.6", {"start": v(40.27, 74.4) * mm, "mid": v(43.26, 73.86) * mm, "end": v(45.75, 75.6) * mm});
            skArc(sketch, "E11.41.0", {"start": v(38.86, 79.36) * mm, "mid": v(39.63, 82.55) * mm, "end": v(39.17, 85.8) * mm});
            skPoint(sketch, "E11.41.1", {"position": v(36.7, 80.35) * mm});
            skPoint(sketch, "E11.41.2", {"position": v(30.92, 82.99) * mm});
            skPoint(sketch, "E11.41.3", {"position": v(42.47, 77.71) * mm});
            skArc(sketch, "E11.41.4", {"start": v(34.53, 81.34) * mm, "mid": v(36.42, 84.02) * mm, "end": v(39.17, 85.8) * mm});
            skArc(sketch, "E11.41.5", {"start": v(40.82, 74.1) * mm, "mid": v(38.75, 76.33) * mm, "end": v(38.86, 79.36) * mm});
            skArc(sketch, "E11.41.6", {"start": v(29.27, 79.38) * mm, "mid": v(32.3, 79.27) * mm, "end": v(34.53, 81.34) * mm});
            skArc(sketch, "E11.42.0", {"start": v(27.17, 84.09) * mm, "mid": v(27.48, 87.35) * mm, "end": v(26.56, 90.5) * mm});
            skPoint(sketch, "E11.42.1", {"position": v(24.88, 84.75) * mm});
            skPoint(sketch, "E11.42.2", {"position": v(18.8, 86.54) * mm});
            skPoint(sketch, "E11.42.3", {"position": v(30.98, 82.96) * mm});
            skArc(sketch, "E11.42.4", {"start": v(22.6, 85.42) * mm, "mid": v(24.1, 88.34) * mm, "end": v(26.56, 90.5) * mm});
            skArc(sketch, "E11.42.5", {"start": v(29.86, 79.16) * mm, "mid": v(27.5, 81.06) * mm, "end": v(27.17, 84.09) * mm});
            skArc(sketch, "E11.42.6", {"start": v(17.67, 82.73) * mm, "mid": v(20.7, 83.06) * mm, "end": v(22.6, 85.42) * mm});
            skArc(sketch, "E11.43.0", {"start": v(14.93, 87.1) * mm, "mid": v(14.77, 90.38) * mm, "end": v(13.4, 93.37) * mm});
            skPoint(sketch, "E11.43.2", {"position": v(6.29, 88.34) * mm});
            skPoint(sketch, "E11.43.3", {"position": v(18.86, 86.53) * mm});
            skArc(sketch, "E11.43.4", {"start": v(10.21, 87.77) * mm, "mid": v(11.28, 90.87) * mm, "end": v(13.4, 93.37) * mm});
            skArc(sketch, "E11.43.5", {"start": v(18.3, 82.6) * mm, "mid": v(15.68, 84.15) * mm, "end": v(14.93, 87.1) * mm});
            skArc(sketch, "E11.43.6", {"start": v(5.72, 84.4) * mm, "mid": v(8.66, 85.16) * mm, "end": v(10.21, 87.77) * mm});
            skPoint(sketch, "E11.center", {"position": v(0, 0) * mm});
            skCircle(sketch, "E12", {"center": v(0, 0) * mm, "radius": 76.83 * mm});
            skCircle(sketch, "E13", {"center": v(0, 0) * mm, "radius": 55 * mm, "construction": true});
            skPoint(sketch, "E14.visualSharp", {"position": v(-8.57, -72.7) * mm});
            skPoint(sketch, "E15.visualSharp", {"position": v(8.57, -72.7) * mm});
            skCircle(sketch, "E16", {"center": v(0, -55) * mm, "radius": 5 * mm});
            skLineSegment(sketch, "E17", {"start": v(-8.54, -45.5) * mm, "end": v(-8.54, -66.46) * mm});
            skArc(sketch, "E18", {"start": v(-18.85, -74.48) * mm, "mid": v(-11.73, -72.99) * mm, "end": v(-8.54, -66.46) * mm});
            skLineSegment(sketch, "E19", {"start": v(-8.54, -45.5) * mm, "end": v(0, -45.5) * mm});
            skLineSegment(sketch, "E20.MirrorCS", {"start": v(8.54, -45.5) * mm, "end": v(8.54, -66.46) * mm});
            skLineSegment(sketch, "E21.MirrorCS", {"start": v(8.54, -45.5) * mm, "end": v(0, -45.5) * mm});
            skArc(sketch, "E22.MirrorCS", {"start": v(18.85, -74.48) * mm, "mid": v(11.73, -72.99) * mm, "end": v(8.54, -66.46) * mm});
            skPoint(sketch, "E23.center", {"position": v(0, -0.14) * mm});
            skArc(sketch, "E24.1.0", {"start": v(65.02, -40.94) * mm, "mid": v(65.8, -33.71) * mm, "end": v(60.57, -28.65) * mm});
            skLineSegment(sketch, "E24.1.1", {"start": v(40.64, -22.18) * mm, "end": v(60.57, -28.65) * mm});
            skLineSegment(sketch, "E24.1.2", {"start": v(40.64, -22.18) * mm, "end": v(43.28, -14.06) * mm});
            skLineSegment(sketch, "E24.1.3", {"start": v(45.92, -5.94) * mm, "end": v(43.28, -14.06) * mm});
            skLineSegment(sketch, "E24.1.4", {"start": v(45.92, -5.94) * mm, "end": v(65.85, -12.41) * mm});
            skArc(sketch, "E24.1.5", {"start": v(76.67, -5.09) * mm, "mid": v(73.05, -11.4) * mm, "end": v(65.85, -12.41) * mm});
            skCircle(sketch, "E24.1.6", {"center": v(52.3, -17) * mm, "radius": 5 * mm});
            skArc(sketch, "E24.2.0", {"start": v(59.03, 49.19) * mm, "mid": v(52.4, 52.16) * mm, "end": v(45.97, 48.75) * mm});
            skLineSegment(sketch, "E24.2.1", {"start": v(33.66, 31.8) * mm, "end": v(45.97, 48.75) * mm});
            skLineSegment(sketch, "E24.2.2", {"start": v(33.66, 31.8) * mm, "end": v(26.75, 36.82) * mm});
            skLineSegment(sketch, "E24.2.3", {"start": v(19.84, 41.84) * mm, "end": v(26.75, 36.82) * mm});
            skLineSegment(sketch, "E24.2.4", {"start": v(19.84, 41.84) * mm, "end": v(32.16, 58.8) * mm});
            skArc(sketch, "E24.2.5", {"start": v(28.53, 71.34) * mm, "mid": v(33.41, 65.95) * mm, "end": v(32.16, 58.8) * mm});
            skCircle(sketch, "E24.2.6", {"center": v(32.33, 44.5) * mm, "radius": 5 * mm});
            skArc(sketch, "E24.3.0", {"start": v(-28.53, 71.34) * mm, "mid": v(-33.41, 65.95) * mm, "end": v(-32.16, 58.8) * mm});
            skLineSegment(sketch, "E24.3.1", {"start": v(-19.84, 41.84) * mm, "end": v(-32.16, 58.8) * mm});
            skLineSegment(sketch, "E24.3.2", {"start": v(-19.84, 41.84) * mm, "end": v(-26.75, 36.82) * mm});
            skLineSegment(sketch, "E24.3.3", {"start": v(-33.66, 31.8) * mm, "end": v(-26.75, 36.82) * mm});
            skLineSegment(sketch, "E24.3.4", {"start": v(-33.66, 31.8) * mm, "end": v(-45.97, 48.75) * mm});
            skArc(sketch, "E24.3.5", {"start": v(-59.03, 49.19) * mm, "mid": v(-52.4, 52.16) * mm, "end": v(-45.97, 48.75) * mm});
            skCircle(sketch, "E24.3.6", {"center": v(-32.33, 44.5) * mm, "radius": 5 * mm});
            skArc(sketch, "E24.4.0", {"start": v(-76.67, -5.09) * mm, "mid": v(-73.05, -11.4) * mm, "end": v(-65.85, -12.41) * mm});
            skLineSegment(sketch, "E24.4.1", {"start": v(-45.92, -5.94) * mm, "end": v(-65.85, -12.41) * mm});
            skLineSegment(sketch, "E24.4.2", {"start": v(-45.92, -5.94) * mm, "end": v(-43.28, -14.06) * mm});
            skLineSegment(sketch, "E24.4.3", {"start": v(-40.64, -22.18) * mm, "end": v(-43.28, -14.06) * mm});
            skLineSegment(sketch, "E24.4.4", {"start": v(-40.64, -22.18) * mm, "end": v(-60.57, -28.65) * mm});
            skArc(sketch, "E24.4.5", {"start": v(-65.02, -40.94) * mm, "mid": v(-65.8, -33.71) * mm, "end": v(-60.57, -28.65) * mm});
            skCircle(sketch, "E24.4.6", {"center": v(-52.3, -17) * mm, "radius": 5 * mm});
            skCircle(sketch, "E25", {"center": v(0, -0.14) * mm, "radius": 80.91 * mm});
            skCircle(sketch, "E26", {"center": v(0, -0.14) * mm, "radius": 55 * mm});
            skCircle(sketch, "E27", {"center": v(0, -0.14) * mm, "radius": 59.12 * mm});
            skLineSegment(sketch, "E28", {"start": v(-1.65, 73.38) * mm, "end": v(-1.65, 62.51) * mm});
            skArc(sketch, "E29", {"start": v(-1.65, 73.38) * mm, "mid": v(-2.7, 75.78) * mm, "end": v(-5.17, 76.66) * mm});
            skArc(sketch, "E30", {"start": v(-5.09, 58.76) * mm, "mid": v(-2.64, 59.97) * mm, "end": v(-1.65, 62.51) * mm});
            skArc(sketch, "E31.MirrorCS", {"start": v(1.65, 73.38) * mm, "mid": v(2.7, 75.78) * mm, "end": v(5.17, 76.66) * mm});
            skLineSegment(sketch, "E32.MirrorCS", {"start": v(1.65, 73.38) * mm, "end": v(1.65, 62.51) * mm});
            skArc(sketch, "E33.MirrorCS", {"start": v(5.09, 58.76) * mm, "mid": v(2.64, 59.97) * mm, "end": v(1.65, 62.51) * mm});
            skSolve(sketch);
        }
        {
            var Q0;
            Q0=qCreatedBy(makeId("Front.planeOp"),FACE);
            var sketch = newSketch(context, id + "F1", { "sketchPlane" : qUnion([Q0])});
            skLineSegment(sketch, "E34", {"start": v(47.58, -60.9) * mm, "end": v(46.68, -61.57) * mm});
            skLineSegment(sketch, "E35", {"start": v(46.68, -61.57) * mm, "end": v(46.33, -61.77) * mm});
            skLineSegment(sketch, "E36", {"start": v(46.33, -61.77) * mm, "end": v(44.46, -63.07) * mm});
            skLineSegment(sketch, "E37", {"start": v(44.46, -63.07) * mm, "end": v(39.14, -66.77) * mm});
            skLineSegment(sketch, "E38", {"start": v(39.14, -66.77) * mm, "end": v(35.3, -69.16) * mm});
            skLineSegment(sketch, "E39", {"start": v(35.3, -69.16) * mm, "end": v(31.9, -71.04) * mm});
            skLineSegment(sketch, "E40", {"start": v(31.9, -71.04) * mm, "end": v(30.35, -71.84) * mm});
            skLineSegment(sketch, "E41", {"start": v(30.35, -71.84) * mm, "end": v(22.34, -75.3) * mm});
            skLineSegment(sketch, "E42", {"start": v(22.34, -75.3) * mm, "end": v(22.17, -75.35) * mm});
            skLineSegment(sketch, "E43", {"start": v(22.17, -75.35) * mm, "end": v(22.07, -74.58) * mm});
            skLineSegment(sketch, "E44", {"start": v(22.07, -74.58) * mm, "end": v(22.07, -71.72) * mm});
            skLineSegment(sketch, "E45", {"start": v(22.07, -71.72) * mm, "end": v(22.12, -71.47) * mm});
            skLineSegment(sketch, "E46", {"start": v(22.12, -71.47) * mm, "end": v(22.61, -70.76) * mm});
            skLineSegment(sketch, "E47", {"start": v(22.61, -70.76) * mm, "end": v(23.29, -70.38) * mm});
            skLineSegment(sketch, "E48", {"start": v(23.29, -70.38) * mm, "end": v(23.76, -69.94) * mm});
            skLineSegment(sketch, "E49", {"start": v(23.76, -69.94) * mm, "end": v(23.92, -69.44) * mm});
            skLineSegment(sketch, "E50", {"start": v(23.92, -69.44) * mm, "end": v(24.68, -68.57) * mm});
            skLineSegment(sketch, "E51", {"start": v(24.68, -68.57) * mm, "end": v(25.2, -67.95) * mm});
            skLineSegment(sketch, "E52", {"start": v(25.2, -67.95) * mm, "end": v(25.53, -66.79) * mm});
            skLineSegment(sketch, "E53", {"start": v(25.53, -66.79) * mm, "end": v(25.9, -66.47) * mm});
            skLineSegment(sketch, "E54", {"start": v(25.9, -66.47) * mm, "end": v(26.95, -66.36) * mm});
            skLineSegment(sketch, "E55", {"start": v(26.95, -66.36) * mm, "end": v(28.16, -66.12) * mm});
            skLineSegment(sketch, "E56", {"start": v(28.16, -66.12) * mm, "end": v(28.4, -66.05) * mm});
            skLineSegment(sketch, "E57", {"start": v(28.4, -66.05) * mm, "end": v(29.14, -66.03) * mm});
            skLineSegment(sketch, "E58", {"start": v(29.14, -66.03) * mm, "end": v(30.5, -66.4) * mm});
            skLineSegment(sketch, "E59", {"start": v(30.5, -66.4) * mm, "end": v(31.1, -66.8) * mm});
            skLineSegment(sketch, "E60", {"start": v(31.1, -66.8) * mm, "end": v(31.53, -67.3) * mm});
            skLineSegment(sketch, "E61", {"start": v(31.53, -67.3) * mm, "end": v(32.4, -68.45) * mm});
            skLineSegment(sketch, "E62", {"start": v(32.4, -68.45) * mm, "end": v(33.6, -67.88) * mm});
            skLineSegment(sketch, "E63", {"start": v(33.6, -67.88) * mm, "end": v(33.88, -67.68) * mm});
            skLineSegment(sketch, "E64", {"start": v(33.88, -67.68) * mm, "end": v(34.07, -67.34) * mm});
            skLineSegment(sketch, "E65", {"start": v(34.07, -67.34) * mm, "end": v(34.75, -61.87) * mm});
            skLineSegment(sketch, "E66", {"start": v(34.75, -61.87) * mm, "end": v(34.78, -60.13) * mm});
            skLineSegment(sketch, "E67", {"start": v(34.78, -60.13) * mm, "end": v(34.3, -59.3) * mm});
            skLineSegment(sketch, "E68", {"start": v(34.3, -59.3) * mm, "end": v(33.8, -59.15) * mm});
            skLineSegment(sketch, "E69", {"start": v(33.8, -59.15) * mm, "end": v(31.55, -59.25) * mm});
            skLineSegment(sketch, "E70", {"start": v(31.55, -59.25) * mm, "end": v(30.77, -59.2) * mm});
            skLineSegment(sketch, "E71", {"start": v(30.77, -59.2) * mm, "end": v(28.23, -58.7) * mm});
            skLineSegment(sketch, "E72", {"start": v(28.23, -58.7) * mm, "end": v(27.52, -58.68) * mm});
            skLineSegment(sketch, "E73", {"start": v(27.52, -58.68) * mm, "end": v(26.55, -59) * mm});
            skLineSegment(sketch, "E74", {"start": v(26.55, -59) * mm, "end": v(24.25, -59.78) * mm});
            skLineSegment(sketch, "E75", {"start": v(24.25, -59.78) * mm, "end": v(22.78, -60.17) * mm});
            skLineSegment(sketch, "E76", {"start": v(22.78, -60.17) * mm, "end": v(21.49, -60.36) * mm});
            skLineSegment(sketch, "E77", {"start": v(21.49, -60.36) * mm, "end": v(21.21, -60.3) * mm});
            skLineSegment(sketch, "E78", {"start": v(21.21, -60.3) * mm, "end": v(19.77, -59.81) * mm});
            skLineSegment(sketch, "E79", {"start": v(19.77, -59.81) * mm, "end": v(19.32, -59.73) * mm});
            skLineSegment(sketch, "E80", {"start": v(19.32, -59.73) * mm, "end": v(17.04, -59.65) * mm});
            skLineSegment(sketch, "E81", {"start": v(17.04, -59.65) * mm, "end": v(15.84, -59.38) * mm});
            skLineSegment(sketch, "E82", {"start": v(15.84, -59.38) * mm, "end": v(15.36, -58.76) * mm});
            skLineSegment(sketch, "E83", {"start": v(15.36, -58.76) * mm, "end": v(15.25, -58.06) * mm});
            skLineSegment(sketch, "E84", {"start": v(15.25, -58.06) * mm, "end": v(14.8, -58.12) * mm});
            skLineSegment(sketch, "E85", {"start": v(14.8, -58.12) * mm, "end": v(10.67, -58.68) * mm});
            skLineSegment(sketch, "E86", {"start": v(10.67, -58.68) * mm, "end": v(7.85, -58.84) * mm});
            skLineSegment(sketch, "E87", {"start": v(7.85, -58.84) * mm, "end": v(5, -58.33) * mm});
            skLineSegment(sketch, "E88", {"start": v(5, -58.33) * mm, "end": v(1.02, -57.07) * mm});
            skLineSegment(sketch, "E89", {"start": v(1.02, -57.07) * mm, "end": v(0, -56.55) * mm});
            skLineSegment(sketch, "E90", {"start": v(0, -56.55) * mm, "end": v(-6.33, -52.06) * mm});
            skLineSegment(sketch, "E91", {"start": v(-6.33, -52.06) * mm, "end": v(-7.15, -51.45) * mm});
            skLineSegment(sketch, "E92", {"start": v(-7.15, -51.45) * mm, "end": v(-10, -48.84) * mm});
            skLineSegment(sketch, "E93", {"start": v(-10, -48.84) * mm, "end": v(-12.96, -46.26) * mm});
            skLineSegment(sketch, "E94", {"start": v(-12.96, -46.26) * mm, "end": v(-14.28, -45.27) * mm});
            skLineSegment(sketch, "E95", {"start": v(-14.28, -45.27) * mm, "end": v(-20.33, -41.84) * mm});
            skLineSegment(sketch, "E96", {"start": v(-20.33, -41.84) * mm, "end": v(-27.37, -38.04) * mm});
            skLineSegment(sketch, "E97", {"start": v(-27.37, -38.04) * mm, "end": v(-28.3, -37.42) * mm});
            skLineSegment(sketch, "E98", {"start": v(-28.3, -37.42) * mm, "end": v(-31.34, -34.88) * mm});
            skLineSegment(sketch, "E99", {"start": v(-31.34, -34.88) * mm, "end": v(-32.4, -34.12) * mm});
            skLineSegment(sketch, "E100", {"start": v(-32.4, -34.12) * mm, "end": v(-35.63, -32.9) * mm});
            skLineSegment(sketch, "E101", {"start": v(-35.63, -32.9) * mm, "end": v(-36.37, -32.38) * mm});
            skLineSegment(sketch, "E102", {"start": v(-36.37, -32.38) * mm, "end": v(-36.58, -32.1) * mm});
            skLineSegment(sketch, "E103", {"start": v(-36.58, -32.1) * mm, "end": v(-36.76, -32) * mm});
            skLineSegment(sketch, "E104", {"start": v(-36.76, -32) * mm, "end": v(-38.16, -32.08) * mm});
            skLineSegment(sketch, "E105", {"start": v(-38.16, -32.08) * mm, "end": v(-38.3, -32.14) * mm});
            skLineSegment(sketch, "E106", {"start": v(-38.3, -32.14) * mm, "end": v(-38.3, -32.08) * mm});
            skLineSegment(sketch, "E107", {"start": v(-38.3, -32.08) * mm, "end": v(-37.98, -31.83) * mm});
            skLineSegment(sketch, "E108", {"start": v(-37.98, -31.83) * mm, "end": v(-37.87, -31.81) * mm});
            skLineSegment(sketch, "E109", {"start": v(-37.87, -31.81) * mm, "end": v(-36.9, -31.25) * mm});
            skLineSegment(sketch, "E110", {"start": v(-36.9, -31.25) * mm, "end": v(-35.15, -30.3) * mm});
            skLineSegment(sketch, "E111", {"start": v(-35.15, -30.3) * mm, "end": v(-30.89, -28.3) * mm});
            skLineSegment(sketch, "E112", {"start": v(-30.89, -28.3) * mm, "end": v(-28.17, -27.13) * mm});
            skLineSegment(sketch, "E113", {"start": v(-28.17, -27.13) * mm, "end": v(-23.7, -25.69) * mm});
            skLineSegment(sketch, "E114", {"start": v(-23.7, -25.69) * mm, "end": v(-22.85, -25.5) * mm});
            skLineSegment(sketch, "E115", {"start": v(-22.85, -25.5) * mm, "end": v(-17.31, -24.6) * mm});
            skLineSegment(sketch, "E116", {"start": v(-17.31, -24.6) * mm, "end": v(-14, -24.54) * mm});
            skLineSegment(sketch, "E117", {"start": v(-14, -24.54) * mm, "end": v(-13.34, -24.69) * mm});
            skLineSegment(sketch, "E118", {"start": v(-13.34, -24.69) * mm, "end": v(-6.63, -26.95) * mm});
            skLineSegment(sketch, "E119", {"start": v(-6.63, -26.95) * mm, "end": v(-5.52, -27.26) * mm});
            skLineSegment(sketch, "E120", {"start": v(-5.52, -27.26) * mm, "end": v(-1.7, -28.06) * mm});
            skLineSegment(sketch, "E121", {"start": v(-1.7, -28.06) * mm, "end": v(-0.44, -28.41) * mm});
            skLineSegment(sketch, "E122", {"start": v(-0.44, -28.41) * mm, "end": v(8.24, -31.37) * mm});
            skLineSegment(sketch, "E123", {"start": v(8.24, -31.37) * mm, "end": v(9.43, -32.02) * mm});
            skLineSegment(sketch, "E124", {"start": v(9.43, -32.02) * mm, "end": v(15.35, -36.65) * mm});
            skLineSegment(sketch, "E125", {"start": v(15.35, -36.65) * mm, "end": v(16.25, -36.89) * mm});
            skLineSegment(sketch, "E126", {"start": v(16.25, -36.89) * mm, "end": v(17.67, -36.67) * mm});
            skLineSegment(sketch, "E127", {"start": v(17.67, -36.67) * mm, "end": v(18.58, -36.3) * mm});
            skLineSegment(sketch, "E128", {"start": v(18.58, -36.3) * mm, "end": v(18.83, -36.11) * mm});
            skLineSegment(sketch, "E129", {"start": v(18.83, -36.11) * mm, "end": v(19.93, -35.29) * mm});
            skLineSegment(sketch, "E130", {"start": v(19.93, -35.29) * mm, "end": v(21.38, -33.7) * mm});
            skLineSegment(sketch, "E131", {"start": v(21.38, -33.7) * mm, "end": v(22.43, -32.86) * mm});
            skLineSegment(sketch, "E132", {"start": v(22.43, -32.86) * mm, "end": v(24.16, -31.93) * mm});
            skLineSegment(sketch, "E133", {"start": v(24.16, -31.93) * mm, "end": v(25.92, -30.86) * mm});
            skLineSegment(sketch, "E134", {"start": v(25.92, -30.86) * mm, "end": v(26.5, -30.31) * mm});
            skLineSegment(sketch, "E135", {"start": v(26.5, -30.31) * mm, "end": v(27.62, -28.7) * mm});
            skLineSegment(sketch, "E136", {"start": v(27.62, -28.7) * mm, "end": v(27.77, -28.36) * mm});
            skLineSegment(sketch, "E137", {"start": v(27.77, -28.36) * mm, "end": v(27.84, -28.03) * mm});
            skLineSegment(sketch, "E138", {"start": v(27.84, -28.03) * mm, "end": v(27.66, -24.92) * mm});
            skLineSegment(sketch, "E139", {"start": v(27.66, -24.92) * mm, "end": v(26.18, -14.74) * mm});
            skLineSegment(sketch, "E140", {"start": v(26.18, -14.74) * mm, "end": v(26.03, -11.04) * mm});
            skLineSegment(sketch, "E141", {"start": v(26.03, -11.04) * mm, "end": v(26.11, -7.96) * mm});
            skLineSegment(sketch, "E142", {"start": v(26.11, -7.96) * mm, "end": v(26.14, -6.74) * mm});
            skLineSegment(sketch, "E143", {"start": v(26.14, -6.74) * mm, "end": v(26.47, -4.87) * mm});
            skLineSegment(sketch, "E144", {"start": v(26.47, -4.87) * mm, "end": v(26.87, -2.4) * mm});
            skLineSegment(sketch, "E145", {"start": v(26.87, -2.4) * mm, "end": v(27.1, 0.64) * mm});
            skLineSegment(sketch, "E146", {"start": v(27.1, 0.64) * mm, "end": v(27.41, 2.86) * mm});
            skLineSegment(sketch, "E147", {"start": v(27.41, 2.86) * mm, "end": v(27.82, 4.78) * mm});
            skLineSegment(sketch, "E148", {"start": v(27.82, 4.78) * mm, "end": v(28.48, 7.73) * mm});
            skLineSegment(sketch, "E149", {"start": v(28.48, 7.73) * mm, "end": v(29.72, 12.56) * mm});
            skLineSegment(sketch, "E150", {"start": v(29.72, 12.56) * mm, "end": v(30.1, 13.5) * mm});
            skLineSegment(sketch, "E151", {"start": v(30.1, 13.5) * mm, "end": v(31.74, 16.02) * mm});
            skLineSegment(sketch, "E152", {"start": v(31.74, 16.02) * mm, "end": v(32.96, 17.46) * mm});
            skLineSegment(sketch, "E153", {"start": v(32.96, 17.46) * mm, "end": v(35.22, 19.65) * mm});
            skLineSegment(sketch, "E154", {"start": v(35.22, 19.65) * mm, "end": v(37.84, 22.4) * mm});
            skLineSegment(sketch, "E155", {"start": v(37.84, 22.4) * mm, "end": v(40.07, 24.43) * mm});
            skLineSegment(sketch, "E156", {"start": v(40.07, 24.43) * mm, "end": v(41.91, 25.66) * mm});
            skLineSegment(sketch, "E157", {"start": v(41.91, 25.66) * mm, "end": v(44.28, 27.05) * mm});
            skLineSegment(sketch, "E158", {"start": v(44.28, 27.05) * mm, "end": v(44.35, 26.95) * mm});
            skLineSegment(sketch, "E159", {"start": v(44.35, 26.95) * mm, "end": v(43.84, 25.75) * mm});
            skLineSegment(sketch, "E160", {"start": v(43.84, 25.75) * mm, "end": v(43.86, 25.55) * mm});
            skLineSegment(sketch, "E161", {"start": v(43.86, 25.55) * mm, "end": v(44.63, 24.7) * mm});
            skLineSegment(sketch, "E162", {"start": v(44.63, 24.7) * mm, "end": v(44.67, 24.62) * mm});
            skLineSegment(sketch, "E163", {"start": v(44.67, 24.62) * mm, "end": v(44.55, 24.56) * mm});
            skLineSegment(sketch, "E164", {"start": v(44.55, 24.56) * mm, "end": v(43.36, 23.8) * mm});
            skLineSegment(sketch, "E165", {"start": v(43.36, 23.8) * mm, "end": v(43.17, 23.64) * mm});
            skLineSegment(sketch, "E166", {"start": v(43.17, 23.64) * mm, "end": v(42.82, 22.75) * mm});
            skLineSegment(sketch, "E167", {"start": v(42.82, 22.75) * mm, "end": v(43.32, 18.82) * mm});
            skLineSegment(sketch, "E168", {"start": v(43.32, 18.82) * mm, "end": v(43.42, 18.24) * mm});
            skLineSegment(sketch, "E169", {"start": v(43.42, 18.24) * mm, "end": v(44.56, 13.67) * mm});
            skLineSegment(sketch, "E170", {"start": v(44.56, 13.67) * mm, "end": v(44.92, 11.78) * mm});
            skLineSegment(sketch, "E171", {"start": v(44.92, 11.78) * mm, "end": v(45.58, 6.9) * mm});
            skLineSegment(sketch, "E172", {"start": v(45.58, 6.9) * mm, "end": v(45.68, 6.31) * mm});
            skLineSegment(sketch, "E173", {"start": v(45.68, 6.31) * mm, "end": v(46.53, 3.77) * mm});
            skLineSegment(sketch, "E174", {"start": v(46.53, 3.77) * mm, "end": v(51.25, -9.7) * mm});
            skLineSegment(sketch, "E175", {"start": v(51.25, -9.7) * mm, "end": v(51.98, -12.1) * mm});
            skLineSegment(sketch, "E176", {"start": v(51.98, -12.1) * mm, "end": v(53.53, -16.55) * mm});
            skLineSegment(sketch, "E177", {"start": v(53.53, -16.55) * mm, "end": v(53.63, -17.53) * mm});
            skLineSegment(sketch, "E178", {"start": v(53.63, -17.53) * mm, "end": v(53.03, -22.14) * mm});
            skLineSegment(sketch, "E179", {"start": v(53.03, -22.14) * mm, "end": v(52.72, -23.08) * mm});
            skLineSegment(sketch, "E180", {"start": v(52.72, -23.08) * mm, "end": v(51.31, -25.57) * mm});
            skLineSegment(sketch, "E181", {"start": v(51.31, -25.57) * mm, "end": v(50.45, -27.54) * mm});
            skLineSegment(sketch, "E182", {"start": v(50.45, -27.54) * mm, "end": v(48.76, -32.6) * mm});
            skLineSegment(sketch, "E183", {"start": v(48.76, -32.6) * mm, "end": v(48.84, -33.37) * mm});
            skLineSegment(sketch, "E184", {"start": v(48.84, -33.37) * mm, "end": v(49.05, -33.75) * mm});
            skLineSegment(sketch, "E185", {"start": v(49.05, -33.75) * mm, "end": v(49, -35.32) * mm});
            skLineSegment(sketch, "E186", {"start": v(49, -35.32) * mm, "end": v(48.78, -35.95) * mm});
            skLineSegment(sketch, "E187", {"start": v(48.78, -35.95) * mm, "end": v(48.86, -36.72) * mm});
            skLineSegment(sketch, "E188", {"start": v(48.86, -36.72) * mm, "end": v(48.82, -37.24) * mm});
            skLineSegment(sketch, "E189", {"start": v(48.82, -37.24) * mm, "end": v(47.99, -39.92) * mm});
            skLineSegment(sketch, "E190", {"start": v(47.99, -39.92) * mm, "end": v(47.78, -40.33) * mm});
            skLineSegment(sketch, "E191", {"start": v(47.78, -40.33) * mm, "end": v(46.9, -41.6) * mm});
            skLineSegment(sketch, "E192", {"start": v(46.9, -41.6) * mm, "end": v(45.67, -43.99) * mm});
            skLineSegment(sketch, "E193", {"start": v(45.67, -43.99) * mm, "end": v(45.55, -44.62) * mm});
            skLineSegment(sketch, "E194", {"start": v(45.55, -44.62) * mm, "end": v(45.6, -46.43) * mm});
            skLineSegment(sketch, "E195", {"start": v(45.6, -46.43) * mm, "end": v(45.95, -47.5) * mm});
            skLineSegment(sketch, "E196", {"start": v(45.95, -47.5) * mm, "end": v(45.98, -47.54) * mm});
            skLineSegment(sketch, "E197", {"start": v(45.98, -47.54) * mm, "end": v(46.42, -47.92) * mm});
            skLineSegment(sketch, "E198", {"start": v(46.42, -47.92) * mm, "end": v(48.1, -48.8) * mm});
            skLineSegment(sketch, "E199", {"start": v(48.1, -48.8) * mm, "end": v(50.93, -50.32) * mm});
            skLineSegment(sketch, "E200", {"start": v(50.93, -50.32) * mm, "end": v(54.74, -51.78) * mm});
            skLineSegment(sketch, "E201", {"start": v(54.74, -51.78) * mm, "end": v(55.04, -51.7) * mm});
            skLineSegment(sketch, "E202", {"start": v(55.04, -51.7) * mm, "end": v(56.68, -50.3) * mm});
            skLineSegment(sketch, "E203", {"start": v(56.68, -50.3) * mm, "end": v(56.86, -50.11) * mm});
            skLineSegment(sketch, "E204", {"start": v(56.86, -50.11) * mm, "end": v(56.54, -49.9) * mm});
            skLineSegment(sketch, "E205", {"start": v(56.54, -49.9) * mm, "end": v(56.1, -49.36) * mm});
            skLineSegment(sketch, "E206", {"start": v(56.1, -49.36) * mm, "end": v(55.8, -48.7) * mm});
            skLineSegment(sketch, "E207", {"start": v(55.8, -48.7) * mm, "end": v(55.75, -47.82) * mm});
            skLineSegment(sketch, "E208", {"start": v(55.75, -47.82) * mm, "end": v(56.06, -47.47) * mm});
            skLineSegment(sketch, "E209", {"start": v(56.06, -47.47) * mm, "end": v(56.58, -46.66) * mm});
            skLineSegment(sketch, "E210", {"start": v(56.58, -46.66) * mm, "end": v(56.56, -46.47) * mm});
            skLineSegment(sketch, "E211", {"start": v(56.56, -46.47) * mm, "end": v(56.48, -45.22) * mm});
            skLineSegment(sketch, "E212", {"start": v(56.48, -45.22) * mm, "end": v(56.52, -44.92) * mm});
            skLineSegment(sketch, "E213", {"start": v(56.52, -44.92) * mm, "end": v(56.86, -44.22) * mm});
            skLineSegment(sketch, "E214", {"start": v(56.86, -44.22) * mm, "end": v(57.23, -43.93) * mm});
            skLineSegment(sketch, "E215", {"start": v(57.23, -43.93) * mm, "end": v(58.31, -43.62) * mm});
            skLineSegment(sketch, "E216", {"start": v(58.31, -43.62) * mm, "end": v(58.74, -43.49) * mm});
            skLineSegment(sketch, "E217", {"start": v(58.74, -43.49) * mm, "end": v(58.77, -43.24) * mm});
            skLineSegment(sketch, "E218", {"start": v(58.77, -43.24) * mm, "end": v(58.84, -42.6) * mm});
            skLineSegment(sketch, "E219", {"start": v(58.84, -42.6) * mm, "end": v(59.33, -42.13) * mm});
            skLineSegment(sketch, "E220", {"start": v(59.33, -42.13) * mm, "end": v(59.46, -42) * mm});
            skLineSegment(sketch, "E221", {"start": v(59.46, -42) * mm, "end": v(60.16, -41.75) * mm});
            skLineSegment(sketch, "E222", {"start": v(60.16, -41.75) * mm, "end": v(60.63, -41.75) * mm});
            skLineSegment(sketch, "E223", {"start": v(60.63, -41.75) * mm, "end": v(61.17, -41.86) * mm});
            skLineSegment(sketch, "E224", {"start": v(61.17, -41.86) * mm, "end": v(62.12, -42.25) * mm});
            skLineSegment(sketch, "E225", {"start": v(62.12, -42.25) * mm, "end": v(62.35, -41.78) * mm});
            skLineSegment(sketch, "E226", {"start": v(62.35, -41.78) * mm, "end": v(63.07, -41.74) * mm});
            skLineSegment(sketch, "E227", {"start": v(63.07, -41.74) * mm, "end": v(63.31, -41.78) * mm});
            skLineSegment(sketch, "E228", {"start": v(63.31, -41.78) * mm, "end": v(64.5, -42.44) * mm});
            skLineSegment(sketch, "E229", {"start": v(64.5, -42.44) * mm, "end": v(65.67, -43.22) * mm});
            skLineSegment(sketch, "E230", {"start": v(65.67, -43.22) * mm, "end": v(66.06, -43.5) * mm});
            skLineSegment(sketch, "E231", {"start": v(66.06, -43.5) * mm, "end": v(65.91, -43.69) * mm});
            skLineSegment(sketch, "E232", {"start": v(65.91, -43.69) * mm, "end": v(62.8, -47.05) * mm});
            skLineSegment(sketch, "E233", {"start": v(62.8, -47.05) * mm, "end": v(58.53, -51.7) * mm});
            skLineSegment(sketch, "E234", {"start": v(58.53, -51.7) * mm, "end": v(57.44, -52.86) * mm});
            skLineSegment(sketch, "E235", {"start": v(57.44, -52.86) * mm, "end": v(53.42, -56.12) * mm});
            skLineSegment(sketch, "E236", {"start": v(53.42, -56.12) * mm, "end": v(48.64, -59.98) * mm});
            skLineSegment(sketch, "E237", {"start": v(48.64, -59.98) * mm, "end": v(47.58, -60.9) * mm});
            skLineSegment(sketch, "E238", {"start": v(20.8, -47.53) * mm, "end": v(21.29, -46.28) * mm});
            skLineSegment(sketch, "E239", {"start": v(21.29, -46.28) * mm, "end": v(22.54, -43.54) * mm});
            skLineSegment(sketch, "E240", {"start": v(22.54, -43.54) * mm, "end": v(23.82, -42.25) * mm});
            skLineSegment(sketch, "E241", {"start": v(23.82, -42.25) * mm, "end": v(25.86, -41.05) * mm});
            skLineSegment(sketch, "E242", {"start": v(25.86, -41.05) * mm, "end": v(27.03, -40.8) * mm});
            skLineSegment(sketch, "E243", {"start": v(27.03, -40.8) * mm, "end": v(28.48, -40.93) * mm});
            skLineSegment(sketch, "E244", {"start": v(28.48, -40.93) * mm, "end": v(28.55, -40.84) * mm});
            skLineSegment(sketch, "E245", {"start": v(28.55, -40.84) * mm, "end": v(29.39, -38.96) * mm});
            skLineSegment(sketch, "E246", {"start": v(29.39, -38.96) * mm, "end": v(30.1, -37.88) * mm});
            skLineSegment(sketch, "E247", {"start": v(30.1, -37.88) * mm, "end": v(31.07, -37.08) * mm});
            skLineSegment(sketch, "E248", {"start": v(31.07, -37.08) * mm, "end": v(31.87, -36.55) * mm});
            skLineSegment(sketch, "E249", {"start": v(31.87, -36.55) * mm, "end": v(33.03, -35.94) * mm});
            skLineSegment(sketch, "E250", {"start": v(33.03, -35.94) * mm, "end": v(34.9, -35.18) * mm});
            skLineSegment(sketch, "E251", {"start": v(34.9, -35.18) * mm, "end": v(36.35, -34.85) * mm});
            skLineSegment(sketch, "E252", {"start": v(36.35, -34.85) * mm, "end": v(37.37, -34.89) * mm});
            skLineSegment(sketch, "E253", {"start": v(37.37, -34.89) * mm, "end": v(39, -35.4) * mm});
            skLineSegment(sketch, "E254", {"start": v(39, -35.4) * mm, "end": v(39.9, -35.82) * mm});
            skLineSegment(sketch, "E255", {"start": v(39.9, -35.82) * mm, "end": v(41.1, -36.56) * mm});
            skLineSegment(sketch, "E256", {"start": v(41.1, -36.56) * mm, "end": v(41.47, -36.77) * mm});
            skLineSegment(sketch, "E257", {"start": v(41.47, -36.77) * mm, "end": v(41.36, -36.12) * mm});
            skLineSegment(sketch, "E258", {"start": v(41.36, -36.12) * mm, "end": v(40.36, -31.72) * mm});
            skLineSegment(sketch, "E259", {"start": v(40.36, -31.72) * mm, "end": v(39.7, -30.92) * mm});
            skLineSegment(sketch, "E260", {"start": v(39.7, -30.92) * mm, "end": v(36.2, -29.42) * mm});
            skLineSegment(sketch, "E261", {"start": v(36.2, -29.42) * mm, "end": v(35.72, -29.2) * mm});
            skLineSegment(sketch, "E262", {"start": v(35.72, -29.2) * mm, "end": v(37.5, -28.5) * mm});
            skLineSegment(sketch, "E263", {"start": v(37.5, -28.5) * mm, "end": v(39.06, -28.3) * mm});
            skLineSegment(sketch, "E264", {"start": v(39.06, -28.3) * mm, "end": v(39.09, -27.95) * mm});
            skLineSegment(sketch, "E265", {"start": v(39.09, -27.95) * mm, "end": v(39.23, -26.17) * mm});
            skLineSegment(sketch, "E266", {"start": v(39.23, -26.17) * mm, "end": v(39.6, -25.14) * mm});
            skLineSegment(sketch, "E267", {"start": v(39.6, -25.14) * mm, "end": v(40.62, -23.68) * mm});
            skLineSegment(sketch, "E268", {"start": v(40.62, -23.68) * mm, "end": v(41.06, -22.56) * mm});
            skLineSegment(sketch, "E269", {"start": v(41.06, -22.56) * mm, "end": v(41.66, -18.74) * mm});
            skLineSegment(sketch, "E270", {"start": v(41.66, -18.74) * mm, "end": v(41.57, -17.54) * mm});
            skLineSegment(sketch, "E271", {"start": v(41.57, -17.54) * mm, "end": v(38.3, -7.6) * mm});
            skLineSegment(sketch, "E272", {"start": v(38.3, -7.6) * mm, "end": v(37.4, -5.07) * mm});
            skLineSegment(sketch, "E273", {"start": v(37.4, -5.07) * mm, "end": v(36.18, -2.4) * mm});
            skLineSegment(sketch, "E274", {"start": v(36.18, -2.4) * mm, "end": v(35.89, -1.2) * mm});
            skLineSegment(sketch, "E275", {"start": v(35.89, -1.2) * mm, "end": v(35.06, 7.41) * mm});
            skLineSegment(sketch, "E276", {"start": v(35.06, 7.41) * mm, "end": v(35.01, 8.25) * mm});
            skLineSegment(sketch, "E277", {"start": v(35.01, 8.25) * mm, "end": v(35.11, 10.78) * mm});
            skLineSegment(sketch, "E278", {"start": v(35.11, 10.78) * mm, "end": v(35.22, 11.52) * mm});
            skLineSegment(sketch, "E279", {"start": v(35.22, 11.52) * mm, "end": v(36.13, 15.37) * mm});
            skLineSegment(sketch, "E280", {"start": v(36.13, 15.37) * mm, "end": v(36.72, 16.84) * mm});
            skLineSegment(sketch, "E281", {"start": v(36.72, 16.84) * mm, "end": v(38.93, 20.63) * mm});
            skLineSegment(sketch, "E282", {"start": v(38.93, 20.63) * mm, "end": v(39.09, 20.95) * mm});
            skLineSegment(sketch, "E283", {"start": v(39.09, 20.95) * mm, "end": v(39.03, 21) * mm});
            skLineSegment(sketch, "E284", {"start": v(39.03, 21) * mm, "end": v(38.6, 20.6) * mm});
            skLineSegment(sketch, "E285", {"start": v(38.6, 20.6) * mm, "end": v(36.6, 18.68) * mm});
            skLineSegment(sketch, "E286", {"start": v(36.6, 18.68) * mm, "end": v(32.94, 14.81) * mm});
            skLineSegment(sketch, "E287", {"start": v(32.94, 14.81) * mm, "end": v(32.43, 13.84) * mm});
            skLineSegment(sketch, "E288", {"start": v(32.43, 13.84) * mm, "end": v(29.98, 2.98) * mm});
            skLineSegment(sketch, "E289", {"start": v(29.98, 2.98) * mm, "end": v(29.8, 1.96) * mm});
            skLineSegment(sketch, "E290", {"start": v(29.8, 1.96) * mm, "end": v(28.73, -11.78) * mm});
            skLineSegment(sketch, "E291", {"start": v(28.73, -11.78) * mm, "end": v(28.74, -12.47) * mm});
            skLineSegment(sketch, "E292", {"start": v(28.74, -12.47) * mm, "end": v(29.85, -19.33) * mm});
            skLineSegment(sketch, "E293", {"start": v(29.85, -19.33) * mm, "end": v(31.03, -24.81) * mm});
            skLineSegment(sketch, "E294", {"start": v(31.03, -24.81) * mm, "end": v(31.19, -25.95) * mm});
            skLineSegment(sketch, "E295", {"start": v(31.19, -25.95) * mm, "end": v(31.25, -27.82) * mm});
            skLineSegment(sketch, "E296", {"start": v(31.25, -27.82) * mm, "end": v(31.38, -28.68) * mm});
            skLineSegment(sketch, "E297", {"start": v(31.38, -28.68) * mm, "end": v(32.52, -30.9) * mm});
            skLineSegment(sketch, "E298", {"start": v(32.52, -30.9) * mm, "end": v(33.4, -31.37) * mm});
            skLineSegment(sketch, "E299", {"start": v(33.4, -31.37) * mm, "end": v(33.93, -31.42) * mm});
            skLineSegment(sketch, "E300", {"start": v(33.93, -31.42) * mm, "end": v(34.68, -31.69) * mm});
            skLineSegment(sketch, "E301", {"start": v(34.68, -31.69) * mm, "end": v(34.78, -32.68) * mm});
            skLineSegment(sketch, "E302", {"start": v(34.78, -32.68) * mm, "end": v(33.89, -32.7) * mm});
            skLineSegment(sketch, "E303", {"start": v(33.89, -32.7) * mm, "end": v(31.46, -32.57) * mm});
            skLineSegment(sketch, "E304", {"start": v(31.46, -32.57) * mm, "end": v(31.12, -32.58) * mm});
            skLineSegment(sketch, "E305", {"start": v(31.12, -32.58) * mm, "end": v(28.52, -33.18) * mm});
            skLineSegment(sketch, "E306", {"start": v(28.52, -33.18) * mm, "end": v(26.84, -33.83) * mm});
            skLineSegment(sketch, "E307", {"start": v(26.84, -33.83) * mm, "end": v(24.22, -35.22) * mm});
            skLineSegment(sketch, "E308", {"start": v(24.22, -35.22) * mm, "end": v(23.82, -35.5) * mm});
            skLineSegment(sketch, "E309", {"start": v(23.82, -35.5) * mm, "end": v(22.94, -36.42) * mm});
            skLineSegment(sketch, "E310", {"start": v(22.94, -36.42) * mm, "end": v(21.73, -37.88) * mm});
            skLineSegment(sketch, "E311", {"start": v(21.73, -37.88) * mm, "end": v(20.41, -39.96) * mm});
            skLineSegment(sketch, "E312", {"start": v(20.41, -39.96) * mm, "end": v(20.03, -40.74) * mm});
            skLineSegment(sketch, "E313", {"start": v(20.03, -40.74) * mm, "end": v(19.31, -42.64) * mm});
            skLineSegment(sketch, "E314", {"start": v(19.31, -42.64) * mm, "end": v(19.17, -43.62) * mm});
            skLineSegment(sketch, "E315", {"start": v(19.17, -43.62) * mm, "end": v(19.37, -46.82) * mm});
            skLineSegment(sketch, "E316", {"start": v(19.37, -46.82) * mm, "end": v(19.4, -47.2) * mm});
            skLineSegment(sketch, "E317", {"start": v(19.4, -47.2) * mm, "end": v(20.8, -47.53) * mm});
            skLineSegment(sketch, "E318", {"start": v(-32.68, -30.89) * mm, "end": v(-32.66, -30.96) * mm});
            skLineSegment(sketch, "E319", {"start": v(-32.66, -30.96) * mm, "end": v(-32.33, -30.94) * mm});
            skLineSegment(sketch, "E320", {"start": v(-32.33, -30.94) * mm, "end": v(-26.39, -30.54) * mm});
            skLineSegment(sketch, "E321", {"start": v(-26.39, -30.54) * mm, "end": v(-25.15, -30.65) * mm});
            skLineSegment(sketch, "E322", {"start": v(-25.15, -30.65) * mm, "end": v(-23.63, -31.01) * mm});
            skLineSegment(sketch, "E323", {"start": v(-23.63, -31.01) * mm, "end": v(-23.23, -31.07) * mm});
            skLineSegment(sketch, "E324", {"start": v(-23.23, -31.07) * mm, "end": v(-21.85, -30.89) * mm});
            skLineSegment(sketch, "E325", {"start": v(-21.85, -30.89) * mm, "end": v(-21.54, -30.85) * mm});
            skLineSegment(sketch, "E326", {"start": v(-21.54, -30.85) * mm, "end": v(-19.91, -31.31) * mm});
            skLineSegment(sketch, "E327", {"start": v(-19.91, -31.31) * mm, "end": v(-19.14, -31.48) * mm});
            skLineSegment(sketch, "E328", {"start": v(-19.14, -31.48) * mm, "end": v(-17.33, -31.66) * mm});
            skLineSegment(sketch, "E329", {"start": v(-17.33, -31.66) * mm, "end": v(-16.1, -32) * mm});
            skLineSegment(sketch, "E330", {"start": v(-16.1, -32) * mm, "end": v(-15.12, -32.4) * mm});
            skLineSegment(sketch, "E331", {"start": v(-15.12, -32.4) * mm, "end": v(-13.74, -33.25) * mm});
            skLineSegment(sketch, "E332", {"start": v(-13.74, -33.25) * mm, "end": v(-12.88, -33.81) * mm});
            skLineSegment(sketch, "E333", {"start": v(-12.88, -33.81) * mm, "end": v(-9.17, -36.54) * mm});
            skLineSegment(sketch, "E334", {"start": v(-9.17, -36.54) * mm, "end": v(-8.82, -36.8) * mm});
            skLineSegment(sketch, "E335", {"start": v(-8.82, -36.8) * mm, "end": v(-5.15, -39.6) * mm});
            skLineSegment(sketch, "E336", {"start": v(-5.15, -39.6) * mm, "end": v(-3.36, -41) * mm});
            skLineSegment(sketch, "E337", {"start": v(-3.36, -41) * mm, "end": v(-1.93, -42.25) * mm});
            skLineSegment(sketch, "E338", {"start": v(-1.93, -42.25) * mm, "end": v(-0.88, -43.22) * mm});
            skLineSegment(sketch, "E339", {"start": v(-0.88, -43.22) * mm, "end": v(1.1, -45.25) * mm});
            skLineSegment(sketch, "E340", {"start": v(1.1, -45.25) * mm, "end": v(2, -45.8) * mm});
            skLineSegment(sketch, "E341", {"start": v(2, -45.8) * mm, "end": v(5.46, -46.67) * mm});
            skLineSegment(sketch, "E342", {"start": v(5.46, -46.67) * mm, "end": v(6.42, -46.8) * mm});
            skLineSegment(sketch, "E343", {"start": v(6.42, -46.8) * mm, "end": v(8.53, -46.75) * mm});
            skLineSegment(sketch, "E344", {"start": v(8.53, -46.75) * mm, "end": v(10.77, -46.59) * mm});
            skLineSegment(sketch, "E345", {"start": v(10.77, -46.59) * mm, "end": v(11.32, -46.34) * mm});
            skLineSegment(sketch, "E346", {"start": v(11.32, -46.34) * mm, "end": v(12.03, -45.56) * mm});
            skLineSegment(sketch, "E347", {"start": v(12.03, -45.56) * mm, "end": v(12.67, -44.9) * mm});
            skLineSegment(sketch, "E348", {"start": v(12.67, -44.9) * mm, "end": v(13, -45.48) * mm});
            skLineSegment(sketch, "E349", {"start": v(13, -45.48) * mm, "end": v(13.07, -46.45) * mm});
            skLineSegment(sketch, "E350", {"start": v(13.07, -46.45) * mm, "end": v(13.35, -47.33) * mm});
            skLineSegment(sketch, "E351", {"start": v(13.35, -47.33) * mm, "end": v(13.92, -47.38) * mm});
            skLineSegment(sketch, "E352", {"start": v(13.92, -47.38) * mm, "end": v(14.67, -46.12) * mm});
            skLineSegment(sketch, "E353", {"start": v(14.67, -46.12) * mm, "end": v(14.75, -45.85) * mm});
            skLineSegment(sketch, "E354", {"start": v(14.75, -45.85) * mm, "end": v(15.4, -42.29) * mm});
            skLineSegment(sketch, "E355", {"start": v(15.4, -42.29) * mm, "end": v(15.39, -42.02) * mm});
            skLineSegment(sketch, "E356", {"start": v(15.39, -42.02) * mm, "end": v(14.73, -40.81) * mm});
            skLineSegment(sketch, "E357", {"start": v(14.73, -40.81) * mm, "end": v(14.63, -40.7) * mm});
            skLineSegment(sketch, "E358", {"start": v(14.63, -40.7) * mm, "end": v(13.8, -39.34) * mm});
            skLineSegment(sketch, "E359", {"start": v(13.8, -39.34) * mm, "end": v(13.09, -38.53) * mm});
            skLineSegment(sketch, "E360", {"start": v(13.09, -38.53) * mm, "end": v(9.21, -35.5) * mm});
            skLineSegment(sketch, "E361", {"start": v(9.21, -35.5) * mm, "end": v(8.12, -34.87) * mm});
            skLineSegment(sketch, "E362", {"start": v(8.12, -34.87) * mm, "end": v(6.22, -34.18) * mm});
            skLineSegment(sketch, "E363", {"start": v(6.22, -34.18) * mm, "end": v(1.51, -32.18) * mm});
            skLineSegment(sketch, "E364", {"start": v(1.51, -32.18) * mm, "end": v(1.14, -32.02) * mm});
            skLineSegment(sketch, "E365", {"start": v(1.14, -32.02) * mm, "end": v(-4.92, -29.7) * mm});
            skLineSegment(sketch, "E366", {"start": v(-4.92, -29.7) * mm, "end": v(-5.9, -29.43) * mm});
            skLineSegment(sketch, "E367", {"start": v(-5.9, -29.43) * mm, "end": v(-9.36, -28.74) * mm});
            skLineSegment(sketch, "E368", {"start": v(-9.36, -28.74) * mm, "end": v(-10.49, -28.39) * mm});
            skLineSegment(sketch, "E369", {"start": v(-10.49, -28.39) * mm, "end": v(-13.64, -27.03) * mm});
            skLineSegment(sketch, "E370", {"start": v(-13.64, -27.03) * mm, "end": v(-14.82, -26.78) * mm});
            skLineSegment(sketch, "E371", {"start": v(-14.82, -26.78) * mm, "end": v(-16.97, -26.73) * mm});
            skLineSegment(sketch, "E372", {"start": v(-16.97, -26.73) * mm, "end": v(-18.14, -26.85) * mm});
            skLineSegment(sketch, "E373", {"start": v(-18.14, -26.85) * mm, "end": v(-20.83, -27.5) * mm});
            skLineSegment(sketch, "E374", {"start": v(-20.83, -27.5) * mm, "end": v(-24.25, -28.33) * mm});
            skLineSegment(sketch, "E375", {"start": v(-24.25, -28.33) * mm, "end": v(-32.15, -30.7) * mm});
            skLineSegment(sketch, "E376", {"start": v(-32.15, -30.7) * mm, "end": v(-32.68, -30.89) * mm});
            skLineSegment(sketch, "E377", {"start": v(47.09, -11.27) * mm, "end": v(47.19, -11.73) * mm});
            skLineSegment(sketch, "E378", {"start": v(47.19, -11.73) * mm, "end": v(48.59, -18.98) * mm});
            skLineSegment(sketch, "E379", {"start": v(48.59, -18.98) * mm, "end": v(48.56, -19.94) * mm});
            skLineSegment(sketch, "E380", {"start": v(48.56, -19.94) * mm, "end": v(47.52, -24.05) * mm});
            skLineSegment(sketch, "E381", {"start": v(47.52, -24.05) * mm, "end": v(47.04, -25.02) * mm});
            skLineSegment(sketch, "E382", {"start": v(47.04, -25.02) * mm, "end": v(46.28, -26) * mm});
            skLineSegment(sketch, "E383", {"start": v(46.28, -26) * mm, "end": v(46, -26.62) * mm});
            skLineSegment(sketch, "E384", {"start": v(46, -26.62) * mm, "end": v(45.8, -28.48) * mm});
            skLineSegment(sketch, "E385", {"start": v(45.8, -28.48) * mm, "end": v(45.94, -29.16) * mm});
            skLineSegment(sketch, "E386", {"start": v(45.94, -29.16) * mm, "end": v(46.74, -30.14) * mm});
            skLineSegment(sketch, "E387", {"start": v(46.74, -30.14) * mm, "end": v(47.27, -29.43) * mm});
            skLineSegment(sketch, "E388", {"start": v(47.27, -29.43) * mm, "end": v(48.05, -27.16) * mm});
            skLineSegment(sketch, "E389", {"start": v(48.05, -27.16) * mm, "end": v(49, -25.27) * mm});
            skLineSegment(sketch, "E390", {"start": v(49, -25.27) * mm, "end": v(49.54, -24.15) * mm});
            skLineSegment(sketch, "E391", {"start": v(49.54, -24.15) * mm, "end": v(50.34, -22.05) * mm});
            skLineSegment(sketch, "E392", {"start": v(50.34, -22.05) * mm, "end": v(50.45, -21.63) * mm});
            skLineSegment(sketch, "E393", {"start": v(50.45, -21.63) * mm, "end": v(51, -18.25) * mm});
            skLineSegment(sketch, "E394", {"start": v(51, -18.25) * mm, "end": v(50.9, -16.77) * mm});
            skLineSegment(sketch, "E395", {"start": v(50.9, -16.77) * mm, "end": v(49.21, -10.9) * mm});
            skLineSegment(sketch, "E396", {"start": v(49.21, -10.9) * mm, "end": v(48, -7) * mm});
            skLineSegment(sketch, "E397", {"start": v(48, -7) * mm, "end": v(44.76, 2) * mm});
            skLineSegment(sketch, "E398", {"start": v(44.76, 2) * mm, "end": v(44.48, 2.95) * mm});
            skLineSegment(sketch, "E399", {"start": v(44.48, 2.95) * mm, "end": v(41.35, 17.7) * mm});
            skLineSegment(sketch, "E400", {"start": v(41.35, 17.7) * mm, "end": v(41.23, 18.47) * mm});
            skLineSegment(sketch, "E401", {"start": v(41.23, 18.47) * mm, "end": v(41.03, 20.33) * mm});
            skLineSegment(sketch, "E402", {"start": v(41.03, 20.33) * mm, "end": v(40.88, 20.78) * mm});
            skLineSegment(sketch, "E403", {"start": v(40.88, 20.78) * mm, "end": v(40.82, 20.55) * mm});
            skLineSegment(sketch, "E404", {"start": v(40.82, 20.55) * mm, "end": v(40.78, 17.63) * mm});
            skLineSegment(sketch, "E405", {"start": v(40.78, 17.63) * mm, "end": v(40.83, 16.11) * mm});
            skLineSegment(sketch, "E406", {"start": v(40.83, 16.11) * mm, "end": v(40.8, 15.36) * mm});
            skLineSegment(sketch, "E407", {"start": v(40.8, 15.36) * mm, "end": v(40.9, 13.6) * mm});
            skLineSegment(sketch, "E408", {"start": v(40.9, 13.6) * mm, "end": v(41.03, 12.45) * mm});
            skLineSegment(sketch, "E409", {"start": v(41.03, 12.45) * mm, "end": v(40.88, 8.84) * mm});
            skLineSegment(sketch, "E410", {"start": v(40.88, 8.84) * mm, "end": v(40.37, 7.67) * mm});
            skLineSegment(sketch, "E411", {"start": v(40.37, 7.67) * mm, "end": v(39.64, 6.94) * mm});
            skLineSegment(sketch, "E412", {"start": v(39.64, 6.94) * mm, "end": v(39.3, 6.58) * mm});
            skLineSegment(sketch, "E413", {"start": v(39.3, 6.58) * mm, "end": v(39.87, 6.44) * mm});
            skLineSegment(sketch, "E414", {"start": v(39.87, 6.44) * mm, "end": v(40.63, 6.41) * mm});
            skLineSegment(sketch, "E415", {"start": v(40.63, 6.41) * mm, "end": v(41.65, 6.62) * mm});
            skLineSegment(sketch, "E416", {"start": v(41.65, 6.62) * mm, "end": v(41.72, 6.37) * mm});
            skLineSegment(sketch, "E417", {"start": v(41.72, 6.37) * mm, "end": v(42.42, 4.14) * mm});
            skLineSegment(sketch, "E418", {"start": v(42.42, 4.14) * mm, "end": v(43.04, 1.45) * mm});
            skLineSegment(sketch, "E419", {"start": v(43.04, 1.45) * mm, "end": v(43.31, -0.11) * mm});
            skLineSegment(sketch, "E420", {"start": v(43.31, -0.11) * mm, "end": v(44.17, -3.04) * mm});
            skLineSegment(sketch, "E421", {"start": v(44.17, -3.04) * mm, "end": v(44.57, -3.99) * mm});
            skLineSegment(sketch, "E422", {"start": v(44.57, -3.99) * mm, "end": v(46, -7.16) * mm});
            skLineSegment(sketch, "E423", {"start": v(46, -7.16) * mm, "end": v(46.23, -7.84) * mm});
            skLineSegment(sketch, "E424", {"start": v(46.23, -7.84) * mm, "end": v(46.58, -9.63) * mm});
            skLineSegment(sketch, "E425", {"start": v(46.58, -9.63) * mm, "end": v(46.33, -10.36) * mm});
            skLineSegment(sketch, "E426", {"start": v(46.33, -10.36) * mm, "end": v(45.55, -11.33) * mm});
            skLineSegment(sketch, "E427", {"start": v(45.55, -11.33) * mm, "end": v(47.09, -11.27) * mm});
            skLineSegment(sketch, "E428", {"start": v(12.7, -55.92) * mm, "end": v(12.53, -55.73) * mm});
            skLineSegment(sketch, "E429", {"start": v(12.53, -55.73) * mm, "end": v(11.15, -54.43) * mm});
            skLineSegment(sketch, "E430", {"start": v(11.15, -54.43) * mm, "end": v(10.41, -54.05) * mm});
            skLineSegment(sketch, "E431", {"start": v(10.41, -54.05) * mm, "end": v(7.55, -53.63) * mm});
            skLineSegment(sketch, "E432", {"start": v(7.55, -53.63) * mm, "end": v(6.55, -53.56) * mm});
            skLineSegment(sketch, "E433", {"start": v(6.55, -53.56) * mm, "end": v(6.16, -53.5) * mm});
            skLineSegment(sketch, "E434", {"start": v(6.16, -53.5) * mm, "end": v(2.88, -52.3) * mm});
            skLineSegment(sketch, "E435", {"start": v(2.88, -52.3) * mm, "end": v(2.04, -51.9) * mm});
            skLineSegment(sketch, "E436", {"start": v(2.04, -51.9) * mm, "end": v(0.97, -51.34) * mm});
            skLineSegment(sketch, "E437", {"start": v(0.97, -51.34) * mm, "end": v(-2.4, -49.27) * mm});
            skLineSegment(sketch, "E438", {"start": v(-2.4, -49.27) * mm, "end": v(-2.88, -48.64) * mm});
            skLineSegment(sketch, "E439", {"start": v(-2.88, -48.64) * mm, "end": v(-3.08, -45.88) * mm});
            skLineSegment(sketch, "E440", {"start": v(-3.08, -45.88) * mm, "end": v(-3.1, -45.58) * mm});
            skLineSegment(sketch, "E441", {"start": v(-3.1, -45.58) * mm, "end": v(-4.52, -47.62) * mm});
            skLineSegment(sketch, "E442", {"start": v(-4.52, -47.62) * mm, "end": v(-4.7, -47.55) * mm});
            skLineSegment(sketch, "E443", {"start": v(-4.7, -47.55) * mm, "end": v(-6.01, -46.66) * mm});
            skLineSegment(sketch, "E444", {"start": v(-6.01, -46.66) * mm, "end": v(-8.22, -44.88) * mm});
            skLineSegment(sketch, "E445", {"start": v(-8.22, -44.88) * mm, "end": v(-10.08, -43.47) * mm});
            skLineSegment(sketch, "E446", {"start": v(-10.08, -43.47) * mm, "end": v(-13.65, -41.24) * mm});
            skLineSegment(sketch, "E447", {"start": v(-13.65, -41.24) * mm, "end": v(-15.96, -39.77) * mm});
            skLineSegment(sketch, "E448", {"start": v(-15.96, -39.77) * mm, "end": v(-21.24, -35.86) * mm});
            skLineSegment(sketch, "E449", {"start": v(-21.24, -35.86) * mm, "end": v(-22.3, -35.4) * mm});
            skLineSegment(sketch, "E450", {"start": v(-22.3, -35.4) * mm, "end": v(-25, -34.94) * mm});
            skLineSegment(sketch, "E451", {"start": v(-25, -34.94) * mm, "end": v(-26.12, -34.58) * mm});
            skLineSegment(sketch, "E452", {"start": v(-26.12, -34.58) * mm, "end": v(-29.6, -32.92) * mm});
            skLineSegment(sketch, "E453", {"start": v(-29.6, -32.92) * mm, "end": v(-30.17, -32.79) * mm});
            skLineSegment(sketch, "E454", {"start": v(-30.17, -32.79) * mm, "end": v(-28.67, -33.9) * mm});
            skLineSegment(sketch, "E455", {"start": v(-28.67, -33.9) * mm, "end": v(-22.87, -37.44) * mm});
            skLineSegment(sketch, "E456", {"start": v(-22.87, -37.44) * mm, "end": v(-16.56, -41.5) * mm});
            skLineSegment(sketch, "E457", {"start": v(-16.56, -41.5) * mm, "end": v(-12.78, -44.08) * mm});
            skLineSegment(sketch, "E458", {"start": v(-12.78, -44.08) * mm, "end": v(-11.03, -45.23) * mm});
            skLineSegment(sketch, "E459", {"start": v(-11.03, -45.23) * mm, "end": v(-8.7, -46.88) * mm});
            skLineSegment(sketch, "E460", {"start": v(-8.7, -46.88) * mm, "end": v(-6.62, -48.77) * mm});
            skLineSegment(sketch, "E461", {"start": v(-6.62, -48.77) * mm, "end": v(-5.53, -49.74) * mm});
            skLineSegment(sketch, "E462", {"start": v(-5.53, -49.74) * mm, "end": v(-2.22, -51.8) * mm});
            skLineSegment(sketch, "E463", {"start": v(-2.22, -51.8) * mm, "end": v(3.17, -54.87) * mm});
            skLineSegment(sketch, "E464", {"start": v(3.17, -54.87) * mm, "end": v(3.97, -55.21) * mm});
            skLineSegment(sketch, "E465", {"start": v(3.97, -55.21) * mm, "end": v(6.06, -55.82) * mm});
            skLineSegment(sketch, "E466", {"start": v(6.06, -55.82) * mm, "end": v(7.7, -56.05) * mm});
            skLineSegment(sketch, "E467", {"start": v(7.7, -56.05) * mm, "end": v(12.15, -55.96) * mm});
            skLineSegment(sketch, "E468", {"start": v(12.15, -55.96) * mm, "end": v(12.7, -55.92) * mm});
            skLineSegment(sketch, "E469", {"start": v(37.3, -49.15) * mm, "end": v(36.72, -49.21) * mm});
            skLineSegment(sketch, "E470", {"start": v(36.72, -49.21) * mm, "end": v(35.94, -49.45) * mm});
            skLineSegment(sketch, "E471", {"start": v(35.94, -49.45) * mm, "end": v(35.21, -50.1) * mm});
            skLineSegment(sketch, "E472", {"start": v(35.21, -50.1) * mm, "end": v(34.65, -50.94) * mm});
            skLineSegment(sketch, "E473", {"start": v(34.65, -50.94) * mm, "end": v(34.26, -51.87) * mm});
            skLineSegment(sketch, "E474", {"start": v(34.26, -51.87) * mm, "end": v(34.2, -52) * mm});
            skLineSegment(sketch, "E475", {"start": v(34.2, -52) * mm, "end": v(33.57, -51.79) * mm});
            skLineSegment(sketch, "E476", {"start": v(33.57, -51.79) * mm, "end": v(32.57, -53.1) * mm});
            skLineSegment(sketch, "E477", {"start": v(32.57, -53.1) * mm, "end": v(32.57, -53.6) * mm});
            skLineSegment(sketch, "E478", {"start": v(32.57, -53.6) * mm, "end": v(33.77, -55.3) * mm});
            skLineSegment(sketch, "E479", {"start": v(33.77, -55.3) * mm, "end": v(34.09, -55.64) * mm});
            skLineSegment(sketch, "E480", {"start": v(34.09, -55.64) * mm, "end": v(34.2, -55.48) * mm});
            skLineSegment(sketch, "E481", {"start": v(34.2, -55.48) * mm, "end": v(35.4, -53.97) * mm});
            skLineSegment(sketch, "E482", {"start": v(35.4, -53.97) * mm, "end": v(35.58, -53.69) * mm});
            skLineSegment(sketch, "E483", {"start": v(35.58, -53.69) * mm, "end": v(35.9, -53.13) * mm});
            skLineSegment(sketch, "E484", {"start": v(35.9, -53.13) * mm, "end": v(36.49, -53.46) * mm});
            skLineSegment(sketch, "E485", {"start": v(36.49, -53.46) * mm, "end": v(37.06, -53.41) * mm});
            skLineSegment(sketch, "E486", {"start": v(37.06, -53.41) * mm, "end": v(37.67, -52.8) * mm});
            skLineSegment(sketch, "E487", {"start": v(37.67, -52.8) * mm, "end": v(38.8, -51.3) * mm});
            skLineSegment(sketch, "E488", {"start": v(38.8, -51.3) * mm, "end": v(39.03, -50.8) * mm});
            skLineSegment(sketch, "E489", {"start": v(39.03, -50.8) * mm, "end": v(39.21, -50.03) * mm});
            skLineSegment(sketch, "E490", {"start": v(39.21, -50.03) * mm, "end": v(39.98, -50.26) * mm});
            skLineSegment(sketch, "E491", {"start": v(39.98, -50.26) * mm, "end": v(40.32, -50.09) * mm});
            skLineSegment(sketch, "E492", {"start": v(40.32, -50.09) * mm, "end": v(41.18, -49.23) * mm});
            skLineSegment(sketch, "E493", {"start": v(41.18, -49.23) * mm, "end": v(41.8, -48.63) * mm});
            skLineSegment(sketch, "E494", {"start": v(41.8, -48.63) * mm, "end": v(40.19, -47.43) * mm});
            skLineSegment(sketch, "E495", {"start": v(40.19, -47.43) * mm, "end": v(38.68, -46.3) * mm});
            skLineSegment(sketch, "E496", {"start": v(38.68, -46.3) * mm, "end": v(37.8, -47.36) * mm});
            skLineSegment(sketch, "E497", {"start": v(37.8, -47.36) * mm, "end": v(36.9, -48.44) * mm});
            skLineSegment(sketch, "E498", {"start": v(36.9, -48.44) * mm, "end": v(37.3, -49.15) * mm});
            skLineSegment(sketch, "E499", {"start": v(11.42, -51.32) * mm, "end": v(12.53, -52.5) * mm});
            skLineSegment(sketch, "E500", {"start": v(12.53, -52.5) * mm, "end": v(13.98, -53.69) * mm});
            skLineSegment(sketch, "E501", {"start": v(13.98, -53.69) * mm, "end": v(14.28, -54) * mm});
            skLineSegment(sketch, "E502", {"start": v(14.28, -54) * mm, "end": v(14.72, -54.67) * mm});
            skLineSegment(sketch, "E503", {"start": v(14.72, -54.67) * mm, "end": v(15.15, -54.99) * mm});
            skLineSegment(sketch, "E504", {"start": v(15.15, -54.99) * mm, "end": v(16.62, -55.48) * mm});
            skLineSegment(sketch, "E505", {"start": v(16.62, -55.48) * mm, "end": v(16.82, -55.58) * mm});
            skLineSegment(sketch, "E506", {"start": v(16.82, -55.58) * mm, "end": v(17.8, -56.63) * mm});
            skLineSegment(sketch, "E507", {"start": v(17.8, -56.63) * mm, "end": v(18.38, -57.17) * mm});
            skLineSegment(sketch, "E508", {"start": v(18.38, -57.17) * mm, "end": v(18.78, -57.3) * mm});
            skLineSegment(sketch, "E509", {"start": v(18.78, -57.3) * mm, "end": v(21.12, -57.27) * mm});
            skLineSegment(sketch, "E510", {"start": v(21.12, -57.27) * mm, "end": v(21.51, -57.32) * mm});
            skLineSegment(sketch, "E511", {"start": v(21.51, -57.32) * mm, "end": v(22.62, -57.65) * mm});
            skLineSegment(sketch, "E512", {"start": v(22.62, -57.65) * mm, "end": v(23.19, -57.62) * mm});
            skLineSegment(sketch, "E513", {"start": v(23.19, -57.62) * mm, "end": v(24.73, -57.34) * mm});
            skLineSegment(sketch, "E514", {"start": v(24.73, -57.34) * mm, "end": v(25.94, -57.14) * mm});
            skLineSegment(sketch, "E515", {"start": v(25.94, -57.14) * mm, "end": v(26.13, -57.03) * mm});
            skLineSegment(sketch, "E516", {"start": v(26.13, -57.03) * mm, "end": v(25.85, -56.83) * mm});
            skLineSegment(sketch, "E517", {"start": v(25.85, -56.83) * mm, "end": v(23.88, -55.58) * mm});
            skLineSegment(sketch, "E518", {"start": v(23.88, -55.58) * mm, "end": v(23.07, -55.26) * mm});
            skLineSegment(sketch, "E519", {"start": v(23.07, -55.26) * mm, "end": v(17.9, -54.16) * mm});
            skLineSegment(sketch, "E520", {"start": v(17.9, -54.16) * mm, "end": v(17.48, -54.01) * mm});
            skLineSegment(sketch, "E521", {"start": v(17.48, -54.01) * mm, "end": v(14.58, -52.58) * mm});
            skLineSegment(sketch, "E522", {"start": v(14.58, -52.58) * mm, "end": v(14.26, -52.38) * mm});
            skLineSegment(sketch, "E523", {"start": v(14.26, -52.38) * mm, "end": v(12.3, -50.9) * mm});
            skLineSegment(sketch, "E524", {"start": v(12.3, -50.9) * mm, "end": v(11.9, -50.62) * mm});
            skLineSegment(sketch, "E525", {"start": v(11.9, -50.62) * mm, "end": v(11.42, -51.32) * mm});
            skLineSegment(sketch, "E526", {"start": v(45.88, -38.26) * mm, "end": v(45.53, -37.49) * mm});
            skLineSegment(sketch, "E527", {"start": v(45.53, -37.49) * mm, "end": v(45.54, -37) * mm});
            skLineSegment(sketch, "E528", {"start": v(45.54, -37) * mm, "end": v(46.11, -35.49) * mm});
            skLineSegment(sketch, "E529", {"start": v(46.11, -35.49) * mm, "end": v(46.08, -35.12) * mm});
            skLineSegment(sketch, "E530", {"start": v(46.08, -35.12) * mm, "end": v(45.78, -34.09) * mm});
            skLineSegment(sketch, "E531", {"start": v(45.78, -34.09) * mm, "end": v(45.28, -32.93) * mm});
            skLineSegment(sketch, "E532", {"start": v(45.28, -32.93) * mm, "end": v(44.98, -32.5) * mm});
            skLineSegment(sketch, "E533", {"start": v(44.98, -32.5) * mm, "end": v(44.25, -30.95) * mm});
            skLineSegment(sketch, "E534", {"start": v(44.25, -30.95) * mm, "end": v(43.67, -30.19) * mm});
            skLineSegment(sketch, "E535", {"start": v(43.67, -30.19) * mm, "end": v(42.73, -29.04) * mm});
            skLineSegment(sketch, "E536", {"start": v(42.73, -29.04) * mm, "end": v(42.42, -28.57) * mm});
            skLineSegment(sketch, "E537", {"start": v(42.42, -28.57) * mm, "end": v(42.23, -28.37) * mm});
            skLineSegment(sketch, "E538", {"start": v(42.23, -28.37) * mm, "end": v(41.05, -27.78) * mm});
            skLineSegment(sketch, "E539", {"start": v(41.05, -27.78) * mm, "end": v(41.18, -28.26) * mm});
            skLineSegment(sketch, "E540", {"start": v(41.18, -28.26) * mm, "end": v(41.9, -30.48) * mm});
            skLineSegment(sketch, "E541", {"start": v(41.9, -30.48) * mm, "end": v(42.92, -34.33) * mm});
            skLineSegment(sketch, "E542", {"start": v(42.92, -34.33) * mm, "end": v(43.6, -38.91) * mm});
            skLineSegment(sketch, "E543", {"start": v(43.6, -38.91) * mm, "end": v(43.71, -39.37) * mm});
            skLineSegment(sketch, "E544", {"start": v(43.71, -39.37) * mm, "end": v(44.43, -41.46) * mm});
            skLineSegment(sketch, "E545", {"start": v(44.43, -41.46) * mm, "end": v(44.55, -41.71) * mm});
            skLineSegment(sketch, "E546", {"start": v(44.55, -41.71) * mm, "end": v(45.88, -38.26) * mm});
            skLineSegment(sketch, "E547", {"start": v(46.51, -51.2) * mm, "end": v(46.5, -51.63) * mm});
            skLineSegment(sketch, "E548", {"start": v(46.5, -51.63) * mm, "end": v(46.52, -53.2) * mm});
            skLineSegment(sketch, "E549", {"start": v(46.52, -53.2) * mm, "end": v(46.4, -54.14) * mm});
            skLineSegment(sketch, "E550", {"start": v(46.4, -54.14) * mm, "end": v(46, -55.59) * mm});
            skLineSegment(sketch, "E551", {"start": v(46, -55.59) * mm, "end": v(45.91, -56) * mm});
            skLineSegment(sketch, "E552", {"start": v(45.91, -56) * mm, "end": v(46.03, -56.04) * mm});
            skLineSegment(sketch, "E553", {"start": v(46.03, -56.04) * mm, "end": v(48.97, -56.3) * mm});
            skLineSegment(sketch, "E554", {"start": v(48.97, -56.3) * mm, "end": v(49.34, -56.18) * mm});
            skLineSegment(sketch, "E555", {"start": v(49.34, -56.18) * mm, "end": v(51.7, -54.34) * mm});
            skLineSegment(sketch, "E556", {"start": v(51.7, -54.34) * mm, "end": v(51.89, -54.18) * mm});
            skLineSegment(sketch, "E557", {"start": v(51.89, -54.18) * mm, "end": v(51.81, -54.1) * mm});
            skLineSegment(sketch, "E558", {"start": v(51.81, -54.1) * mm, "end": v(46.51, -51.2) * mm});
            skLineSegment(sketch, "E559", {"start": v(31.67, -40.7) * mm, "end": v(32.5, -41.92) * mm});
            skLineSegment(sketch, "E560", {"start": v(32.5, -41.92) * mm, "end": v(33.64, -42.97) * mm});
            skLineSegment(sketch, "E561", {"start": v(33.64, -42.97) * mm, "end": v(34.5, -43.5) * mm});
            skLineSegment(sketch, "E562", {"start": v(34.5, -43.5) * mm, "end": v(33.84, -42.15) * mm});
            skLineSegment(sketch, "E563", {"start": v(33.84, -42.15) * mm, "end": v(34.35, -42.06) * mm});
            skLineSegment(sketch, "E564", {"start": v(34.35, -42.06) * mm, "end": v(34.63, -41.94) * mm});
            skLineSegment(sketch, "E565", {"start": v(34.63, -41.94) * mm, "end": v(35.13, -41.52) * mm});
            skLineSegment(sketch, "E566", {"start": v(35.13, -41.52) * mm, "end": v(35.28, -41.17) * mm});
            skLineSegment(sketch, "E567", {"start": v(35.28, -41.17) * mm, "end": v(35.23, -40.4) * mm});
            skLineSegment(sketch, "E568", {"start": v(35.23, -40.4) * mm, "end": v(34.98, -39.9) * mm});
            skLineSegment(sketch, "E569", {"start": v(34.98, -39.9) * mm, "end": v(34.34, -39.34) * mm});
            skLineSegment(sketch, "E570", {"start": v(34.34, -39.34) * mm, "end": v(35.52, -38.23) * mm});
            skLineSegment(sketch, "E571", {"start": v(35.52, -38.23) * mm, "end": v(35.9, -37.56) * mm});
            skLineSegment(sketch, "E572", {"start": v(35.9, -37.56) * mm, "end": v(35.9, -37.42) * mm});
            skLineSegment(sketch, "E573", {"start": v(35.9, -37.42) * mm, "end": v(35.53, -36.88) * mm});
            skLineSegment(sketch, "E574", {"start": v(35.53, -36.88) * mm, "end": v(34.21, -37.8) * mm});
            skLineSegment(sketch, "E575", {"start": v(34.21, -37.8) * mm, "end": v(32.76, -39.02) * mm});
            skLineSegment(sketch, "E576", {"start": v(32.76, -39.02) * mm, "end": v(31.67, -40.7) * mm});
            skLineSegment(sketch, "E577", {"start": v(26.22, -44.48) * mm, "end": v(25.87, -44.7) * mm});
            skLineSegment(sketch, "E578", {"start": v(25.87, -44.7) * mm, "end": v(24.38, -45.77) * mm});
            skLineSegment(sketch, "E579", {"start": v(24.38, -45.77) * mm, "end": v(23.82, -46.3) * mm});
            skLineSegment(sketch, "E580", {"start": v(23.82, -46.3) * mm, "end": v(22.8, -47.34) * mm});
            skLineSegment(sketch, "E581", {"start": v(22.8, -47.34) * mm, "end": v(22.4, -48.45) * mm});
            skLineSegment(sketch, "E582", {"start": v(22.4, -48.45) * mm, "end": v(23.22, -49.62) * mm});
            skLineSegment(sketch, "E583", {"start": v(23.22, -49.62) * mm, "end": v(24.4, -50.69) * mm});
            skLineSegment(sketch, "E584", {"start": v(24.4, -50.69) * mm, "end": v(25.15, -51.14) * mm});
            skLineSegment(sketch, "E585", {"start": v(25.15, -51.14) * mm, "end": v(24.49, -49.78) * mm});
            skLineSegment(sketch, "E586", {"start": v(24.49, -49.78) * mm, "end": v(25.35, -49.59) * mm});
            skLineSegment(sketch, "E587", {"start": v(25.35, -49.59) * mm, "end": v(25.8, -49.12) * mm});
            skLineSegment(sketch, "E588", {"start": v(25.8, -49.12) * mm, "end": v(25.92, -48.48) * mm});
            skLineSegment(sketch, "E589", {"start": v(25.92, -48.48) * mm, "end": v(25.78, -47.94) * mm});
            skLineSegment(sketch, "E590", {"start": v(25.78, -47.94) * mm, "end": v(25.02, -46.93) * mm});
            skLineSegment(sketch, "E591", {"start": v(25.02, -46.93) * mm, "end": v(25.27, -46.68) * mm});
            skLineSegment(sketch, "E592", {"start": v(25.27, -46.68) * mm, "end": v(26.25, -45.77) * mm});
            skLineSegment(sketch, "E593", {"start": v(26.25, -45.77) * mm, "end": v(26.43, -45.05) * mm});
            skLineSegment(sketch, "E594", {"start": v(26.43, -45.05) * mm, "end": v(26.22, -44.48) * mm});
            skLineSegment(sketch, "E595", {"start": v(35.9, -46.94) * mm, "end": v(35.26, -46.3) * mm});
            skLineSegment(sketch, "E596", {"start": v(35.26, -46.3) * mm, "end": v(34.66, -45.98) * mm});
            skLineSegment(sketch, "E597", {"start": v(34.66, -45.98) * mm, "end": v(33.94, -45.81) * mm});
            skLineSegment(sketch, "E598", {"start": v(33.94, -45.81) * mm, "end": v(33.3, -45.96) * mm});
            skLineSegment(sketch, "E599", {"start": v(33.3, -45.96) * mm, "end": v(32.56, -46.66) * mm});
            skLineSegment(sketch, "E600", {"start": v(32.56, -46.66) * mm, "end": v(31.85, -47.41) * mm});
            skLineSegment(sketch, "E601", {"start": v(31.85, -47.41) * mm, "end": v(31.44, -48.42) * mm});
            skLineSegment(sketch, "E602", {"start": v(31.44, -48.42) * mm, "end": v(31.63, -49.49) * mm});
            skLineSegment(sketch, "E603", {"start": v(31.63, -49.49) * mm, "end": v(31.76, -49.62) * mm});
            skLineSegment(sketch, "E604", {"start": v(31.76, -49.62) * mm, "end": v(32.43, -49.86) * mm});
            skLineSegment(sketch, "E605", {"start": v(32.43, -49.86) * mm, "end": v(33.23, -49.5) * mm});
            skLineSegment(sketch, "E606", {"start": v(33.23, -49.5) * mm, "end": v(33.9, -49.15) * mm});
            skLineSegment(sketch, "E607", {"start": v(33.9, -49.15) * mm, "end": v(34.79, -48.68) * mm});
            skLineSegment(sketch, "E608", {"start": v(34.79, -48.68) * mm, "end": v(35.9, -46.94) * mm});
            skLineSegment(sketch, "E609", {"start": v(46.47, -58.8) * mm, "end": v(46.1, -58.68) * mm});
            skLineSegment(sketch, "E610", {"start": v(46.1, -58.68) * mm, "end": v(43.95, -58.08) * mm});
            skLineSegment(sketch, "E611", {"start": v(43.95, -58.08) * mm, "end": v(43.58, -58.03) * mm});
            skLineSegment(sketch, "E612", {"start": v(43.58, -58.03) * mm, "end": v(42.78, -58.07) * mm});
            skLineSegment(sketch, "E613", {"start": v(42.78, -58.07) * mm, "end": v(42.1, -58.42) * mm});
            skLineSegment(sketch, "E614", {"start": v(42.1, -58.42) * mm, "end": v(42.04, -58.53) * mm});
            skLineSegment(sketch, "E615", {"start": v(42.04, -58.53) * mm, "end": v(42.03, -59.36) * mm});
            skLineSegment(sketch, "E616", {"start": v(42.03, -59.36) * mm, "end": v(42.6, -62) * mm});
            skLineSegment(sketch, "E617", {"start": v(42.6, -62) * mm, "end": v(42.64, -62.04) * mm});
            skLineSegment(sketch, "E618", {"start": v(42.64, -62.04) * mm, "end": v(43.11, -61.56) * mm});
            skLineSegment(sketch, "E619", {"start": v(43.11, -61.56) * mm, "end": v(44.07, -60.74) * mm});
            skLineSegment(sketch, "E620", {"start": v(44.07, -60.74) * mm, "end": v(45.38, -60.08) * mm});
            skLineSegment(sketch, "E621", {"start": v(45.38, -60.08) * mm, "end": v(45.55, -59.97) * mm});
            skLineSegment(sketch, "E622", {"start": v(45.55, -59.97) * mm, "end": v(46.47, -58.8) * mm});
            skLineSegment(sketch, "E623", {"start": v(37.12, -60.84) * mm, "end": v(37.2, -62.99) * mm});
            skLineSegment(sketch, "E624", {"start": v(37.2, -62.99) * mm, "end": v(37.41, -65.14) * mm});
            skLineSegment(sketch, "E625", {"start": v(37.41, -65.14) * mm, "end": v(39.44, -63.62) * mm});
            skLineSegment(sketch, "E626", {"start": v(39.44, -63.62) * mm, "end": v(39.58, -63.29) * mm});
            skLineSegment(sketch, "E627", {"start": v(39.58, -63.29) * mm, "end": v(39.83, -61.18) * mm});
            skLineSegment(sketch, "E628", {"start": v(39.83, -61.18) * mm, "end": v(39.85, -60.9) * mm});
            skLineSegment(sketch, "E629", {"start": v(39.85, -60.9) * mm, "end": v(37.12, -60.84) * mm});
            skLineSegment(sketch, "E630", {"start": v(37.17, -38.47) * mm, "end": v(37.1, -38.48) * mm});
            skLineSegment(sketch, "E631", {"start": v(37.1, -38.48) * mm, "end": v(37.09, -38.82) * mm});
            skLineSegment(sketch, "E632", {"start": v(37.09, -38.82) * mm, "end": v(37.1, -39.81) * mm});
            skLineSegment(sketch, "E633", {"start": v(37.1, -39.81) * mm, "end": v(36.72, -42.02) * mm});
            skLineSegment(sketch, "E634", {"start": v(36.72, -42.02) * mm, "end": v(36.03, -43.19) * mm});
            skLineSegment(sketch, "E635", {"start": v(36.03, -43.19) * mm, "end": v(35.78, -44) * mm});
            skLineSegment(sketch, "E636", {"start": v(35.78, -44) * mm, "end": v(36.58, -44.08) * mm});
            skLineSegment(sketch, "E637", {"start": v(36.58, -44.08) * mm, "end": v(36.8, -44.01) * mm});
            skLineSegment(sketch, "E638", {"start": v(36.8, -44.01) * mm, "end": v(37.86, -43.35) * mm});
            skLineSegment(sketch, "E639", {"start": v(37.86, -43.35) * mm, "end": v(38.02, -43.13) * mm});
            skLineSegment(sketch, "E640", {"start": v(38.02, -43.13) * mm, "end": v(38.35, -41.65) * mm});
            skLineSegment(sketch, "E641", {"start": v(38.35, -41.65) * mm, "end": v(38.33, -40.97) * mm});
            skLineSegment(sketch, "E642", {"start": v(38.33, -40.97) * mm, "end": v(38.1, -40.1) * mm});
            skLineSegment(sketch, "E643", {"start": v(38.1, -40.1) * mm, "end": v(37.17, -38.47) * mm});
            skLineSegment(sketch, "E644", {"start": v(28.27, -46.02) * mm, "end": v(28.17, -46.02) * mm});
            skLineSegment(sketch, "E645", {"start": v(28.17, -46.02) * mm, "end": v(28.2, -46.22) * mm});
            skLineSegment(sketch, "E646", {"start": v(28.2, -46.22) * mm, "end": v(27.95, -48.8) * mm});
            skLineSegment(sketch, "E647", {"start": v(27.95, -48.8) * mm, "end": v(27.8, -49.36) * mm});
            skLineSegment(sketch, "E648", {"start": v(27.8, -49.36) * mm, "end": v(27.42, -50.04) * mm});
            skLineSegment(sketch, "E649", {"start": v(27.42, -50.04) * mm, "end": v(27.13, -50.23) * mm});
            skLineSegment(sketch, "E650", {"start": v(27.13, -50.23) * mm, "end": v(26.65, -50.34) * mm});
            skLineSegment(sketch, "E651", {"start": v(26.65, -50.34) * mm, "end": v(26.42, -51.3) * mm});
            skLineSegment(sketch, "E652", {"start": v(26.42, -51.3) * mm, "end": v(27.76, -51.32) * mm});
            skLineSegment(sketch, "E653", {"start": v(27.76, -51.32) * mm, "end": v(27.88, -51.3) * mm});
            skLineSegment(sketch, "E654", {"start": v(27.88, -51.3) * mm, "end": v(29.03, -50.22) * mm});
            skLineSegment(sketch, "E655", {"start": v(29.03, -50.22) * mm, "end": v(29.34, -49.19) * mm});
            skLineSegment(sketch, "E656", {"start": v(29.34, -49.19) * mm, "end": v(29.1, -47.99) * mm});
            skLineSegment(sketch, "E657", {"start": v(29.1, -47.99) * mm, "end": v(28.98, -47.7) * mm});
            skLineSegment(sketch, "E658", {"start": v(28.98, -47.7) * mm, "end": v(28.27, -46.02) * mm});
            skLineSegment(sketch, "E659", {"start": v(60.84, -46.36) * mm, "end": v(59.61, -45.36) * mm});
            skLineSegment(sketch, "E660", {"start": v(59.61, -45.36) * mm, "end": v(59.44, -45.3) * mm});
            skLineSegment(sketch, "E661", {"start": v(59.44, -45.3) * mm, "end": v(58.68, -45.2) * mm});
            skLineSegment(sketch, "E662", {"start": v(58.68, -45.2) * mm, "end": v(58.25, -46.2) * mm});
            skLineSegment(sketch, "E663", {"start": v(58.25, -46.2) * mm, "end": v(58.3, -46.82) * mm});
            skLineSegment(sketch, "E664", {"start": v(58.3, -46.82) * mm, "end": v(58.96, -47.8) * mm});
            skLineSegment(sketch, "E665", {"start": v(58.96, -47.8) * mm, "end": v(59.11, -47.97) * mm});
            skLineSegment(sketch, "E666", {"start": v(59.11, -47.97) * mm, "end": v(60.84, -46.36) * mm});
            skLineSegment(sketch, "E667", {"start": v(62.8, -44.58) * mm, "end": v(62.7, -44.47) * mm});
            skLineSegment(sketch, "E668", {"start": v(62.7, -44.47) * mm, "end": v(61.47, -43.62) * mm});
            skLineSegment(sketch, "E669", {"start": v(61.47, -43.62) * mm, "end": v(60.79, -43.5) * mm});
            skLineSegment(sketch, "E670", {"start": v(60.79, -43.5) * mm, "end": v(60.52, -43.92) * mm});
            skLineSegment(sketch, "E671", {"start": v(60.52, -43.92) * mm, "end": v(60.48, -44) * mm});
            skLineSegment(sketch, "E672", {"start": v(60.48, -44) * mm, "end": v(60.5, -44.42) * mm});
            skLineSegment(sketch, "E673", {"start": v(60.5, -44.42) * mm, "end": v(60.82, -44.95) * mm});
            skLineSegment(sketch, "E674", {"start": v(60.82, -44.95) * mm, "end": v(61.48, -45.83) * mm});
            skLineSegment(sketch, "E675", {"start": v(61.48, -45.83) * mm, "end": v(62.8, -44.58) * mm});
            skLineSegment(sketch, "E676", {"start": v(39.55, -57.45) * mm, "end": v(36.7, -58.98) * mm});
            skLineSegment(sketch, "E677", {"start": v(36.7, -58.98) * mm, "end": v(38.2, -59.2) * mm});
            skLineSegment(sketch, "E678", {"start": v(38.2, -59.2) * mm, "end": v(39.72, -59.08) * mm});
            skLineSegment(sketch, "E679", {"start": v(39.72, -59.08) * mm, "end": v(39.55, -57.45) * mm});
            skLineSegment(sketch, "E680", {"start": v(28.82, -70.13) * mm, "end": v(28.05, -69.1) * mm});
            skLineSegment(sketch, "E681", {"start": v(28.05, -69.1) * mm, "end": v(27.23, -68.47) * mm});
            skLineSegment(sketch, "E682", {"start": v(27.23, -68.47) * mm, "end": v(27.1, -69.76) * mm});
            skLineSegment(sketch, "E683", {"start": v(27.1, -69.76) * mm, "end": v(27.37, -71.02) * mm});
            skLineSegment(sketch, "E684", {"start": v(27.37, -71.02) * mm, "end": v(28.82, -70.13) * mm});
            skLineSegment(sketch, "E685", {"start": v(29.6, -69.57) * mm, "end": v(31.58, -68.7) * mm});
            skLineSegment(sketch, "E686", {"start": v(31.58, -68.7) * mm, "end": v(30.32, -67.87) * mm});
            skLineSegment(sketch, "E687", {"start": v(30.32, -67.87) * mm, "end": v(30.03, -67.9) * mm});
            skLineSegment(sketch, "E688", {"start": v(30.03, -67.9) * mm, "end": v(29.33, -68.42) * mm});
            skLineSegment(sketch, "E689", {"start": v(29.33, -68.42) * mm, "end": v(29.6, -69.57) * mm});
            skLineSegment(sketch, "E690", {"start": v(43.52, -55.23) * mm, "end": v(43.58, -55.17) * mm});
            skLineSegment(sketch, "E691", {"start": v(43.58, -55.17) * mm, "end": v(44.32, -53.08) * mm});
            skLineSegment(sketch, "E692", {"start": v(44.32, -53.08) * mm, "end": v(44.52, -52.12) * mm});
            skLineSegment(sketch, "E693", {"start": v(44.52, -52.12) * mm, "end": v(42.79, -53.84) * mm});
            skLineSegment(sketch, "E694", {"start": v(42.79, -53.84) * mm, "end": v(43.52, -55.23) * mm});
            skLineSegment(sketch, "E695", {"start": v(25.33, -70.95) * mm, "end": v(25.5, -71.72) * mm});
            skLineSegment(sketch, "E696", {"start": v(25.5, -71.72) * mm, "end": v(26.4, -71.38) * mm});
            skLineSegment(sketch, "E697", {"start": v(26.4, -71.38) * mm, "end": v(25.9, -70.85) * mm});
            skLineSegment(sketch, "E698", {"start": v(25.9, -70.85) * mm, "end": v(25.33, -70.95) * mm});
            skSolve(sketch);
        }
        {
            var Q0;
            {var subQ82=sQuery(id+"F0.wireOp",EDGE,"E4.trimOffspring");Q0=makeQuery(id+"F0.imprint","IMPRINT",FACE,{"disambiguationData":[TD([[makeQuery(id+"F0.imprint","IMPRINT",EDGE,{"derivedFrom":subQ82}),-1.0]])]});}
            extrude(context, id + "F2", {"entities" : qUnion([Q0]), "endBound" : BoundingType.SYMMETRIC, "depth" : 2.03 * mm});
        }
        {
            var Q0;
            Q0=makeQuery(id+"F0.imprint","IMPRINT",FACE,{"disambiguationData":[TD([[makeQuery(id+"F0.imprint","IMPRINT",EDGE,{"derivedFrom":sQuery(id+"F0.wireOp",EDGE,"E25")}),1.0]])]});
            var Q1;
            {var subQ0=sQuery(id+"F0.wireOp",EDGE,"E24.4.0");Q1=makeQuery(id+"F0.imprint","IMPRINT",FACE,{"disambiguationData":[TD([[makeQuery(id+"F0.imprint","IMPRINT",EDGE,{"derivedFrom":subQ0}),-1.0]])]});}
            var Q2;
            {var subQ0=sQuery(id+"F0.wireOp",EDGE,"E24.3.0");Q2=makeQuery(id+"F0.imprint","IMPRINT",FACE,{"disambiguationData":[TD([[makeQuery(id+"F0.imprint","IMPRINT",EDGE,{"derivedFrom":subQ0}),-1.0]])]});}
            var Q3;
            {var subQ0=sQuery(id+"F0.wireOp",EDGE,"E24.2.0");Q3=makeQuery(id+"F0.imprint","IMPRINT",FACE,{"disambiguationData":[TD([[makeQuery(id+"F0.imprint","IMPRINT",EDGE,{"derivedFrom":subQ0}),-1.0]])]});}
            var Q4;
            {var subQ0=sQuery(id+"F0.wireOp",EDGE,"E24.1.0");Q4=makeQuery(id+"F0.imprint","IMPRINT",FACE,{"disambiguationData":[TD([[makeQuery(id+"F0.imprint","IMPRINT",EDGE,{"derivedFrom":subQ0}),-1.0]])]});}
            var Q5;
            Q5=makeQuery(id+"F0.imprint","IMPRINT",FACE,{"disambiguationData":[TD([[makeQuery(id+"F0.imprint","IMPRINT",EDGE,{"derivedFrom":sQuery(id+"F0.wireOp",EDGE,"E16")}),-1.0]])]});
            var Q6;
            {var subQ0=sQuery(id+"F0.wireOp",EDGE,"E26");var subQ1=sQuery(id+"F0.wireOp",EDGE,"E24.4.1");var subQ2=makeQuery(id+"F0.imprint","INTERSECT",VERTEX,{"derivedFrom":[subQ1,subQ0]});Q6=makeQuery(id+"F0.imprint","IMPRINT",FACE,{"disambiguationData":[TD([[makeQuery(id+"F0.imprint","IMPRINT",EDGE,{"disambiguationData":[TD([[subQ2,-1.0]])],"derivedFrom":subQ1}),1.0]])]});}
            var Q7;
            {var subQ0=sQuery(id+"F0.wireOp",EDGE,"E26");var subQ1=sQuery(id+"F0.wireOp",EDGE,"E24.3.4");var subQ2=makeQuery(id+"F0.imprint","INTERSECT",VERTEX,{"derivedFrom":[subQ1,subQ0]});Q7=makeQuery(id+"F0.imprint","IMPRINT",FACE,{"disambiguationData":[TD([[makeQuery(id+"F0.imprint","IMPRINT",EDGE,{"disambiguationData":[TD([[subQ2,-1.0]])],"derivedFrom":subQ1}),1.0]])]});}
            var Q8;
            {var subQ1=sQuery(id+"F0.wireOp",EDGE,"E24.4.2");Q8=makeQuery(id+"F0.imprint","IMPRINT",FACE,{"disambiguationData":[TD([[makeQuery(id+"F0.imprint","IMPRINT",EDGE,{"derivedFrom":subQ1}),-1.0]])]});}
            var Q9;
            {var subQ0=sQuery(id+"F0.wireOp",EDGE,"E26");var subQ1=sQuery(id+"F0.wireOp",EDGE,"E17");var subQ2=makeQuery(id+"F0.imprint","INTERSECT",VERTEX,{"derivedFrom":[subQ1,subQ0]});Q9=makeQuery(id+"F0.imprint","IMPRINT",FACE,{"disambiguationData":[TD([[makeQuery(id+"F0.imprint","IMPRINT",EDGE,{"disambiguationData":[TD([[subQ2,-1.0]])],"derivedFrom":subQ1}),-1.0]])]});}
            var Q10;
            {var subQ0=sQuery(id+"F0.wireOp",EDGE,"E18");Q10=makeQuery(id+"F0.imprint","IMPRINT",FACE,{"disambiguationData":[TD([[makeQuery(id+"F0.imprint","IMPRINT",EDGE,{"derivedFrom":subQ0}),-1.0]])]});}
            var Q11;
            {var subQ0=sQuery(id+"F0.wireOp",EDGE,"E26");var subQ1=sQuery(id+"F0.wireOp",EDGE,"E24.4.4");var subQ2=makeQuery(id+"F0.imprint","INTERSECT",VERTEX,{"derivedFrom":[subQ1,subQ0]});Q11=makeQuery(id+"F0.imprint","IMPRINT",FACE,{"disambiguationData":[TD([[makeQuery(id+"F0.imprint","IMPRINT",EDGE,{"disambiguationData":[TD([[subQ2,-1.0]])],"derivedFrom":subQ1}),-1.0]])]});}
            var Q12;
            {var subQ0=sQuery(id+"F0.wireOp",EDGE,"E26");var subQ1=sQuery(id+"F0.wireOp",EDGE,"E24.3.4");var subQ2=makeQuery(id+"F0.imprint","INTERSECT",VERTEX,{"derivedFrom":[subQ1,subQ0]});Q12=makeQuery(id+"F0.imprint","IMPRINT",FACE,{"disambiguationData":[TD([[makeQuery(id+"F0.imprint","IMPRINT",EDGE,{"disambiguationData":[TD([[subQ2,-1.0]])],"derivedFrom":subQ1}),-1.0]])]});}
            var Q13;
            {var subQ0=sQuery(id+"F0.wireOp",EDGE,"E26");var subQ1=sQuery(id+"F0.wireOp",EDGE,"E24.3.1");var subQ2=makeQuery(id+"F0.imprint","INTERSECT",VERTEX,{"derivedFrom":[subQ1,subQ0]});Q13=makeQuery(id+"F0.imprint","IMPRINT",FACE,{"disambiguationData":[TD([[makeQuery(id+"F0.imprint","IMPRINT",EDGE,{"disambiguationData":[TD([[subQ2,-1.0]])],"derivedFrom":subQ1}),1.0]])]});}
            var Q14;
            {var subQ1=sQuery(id+"F0.wireOp",EDGE,"E24.3.2");Q14=makeQuery(id+"F0.imprint","IMPRINT",FACE,{"disambiguationData":[TD([[makeQuery(id+"F0.imprint","IMPRINT",EDGE,{"derivedFrom":subQ1}),-1.0]])]});}
            var Q15;
            Q15=makeQuery(id+"F0.imprint","IMPRINT",FACE,{"disambiguationData":[TD([[makeQuery(id+"F0.imprint","IMPRINT",EDGE,{"derivedFrom":sQuery(id+"F0.wireOp",EDGE,"E28")}),1.0]])]});
            var Q16;
            {var subQ2=sQuery(id+"F0.wireOp",EDGE,"E24.2.4");var subQ4=sQuery(id+"F0.wireOp",EDGE,"E26");var subQ5=makeQuery(id+"F0.imprint","INTERSECT",VERTEX,{"derivedFrom":[subQ2,subQ4]});Q16=makeQuery(id+"F0.imprint","IMPRINT",FACE,{"disambiguationData":[TD([[makeQuery(id+"F0.imprint","IMPRINT",EDGE,{"disambiguationData":[TD([[subQ5,-1.0]])],"derivedFrom":subQ2}),1.0]])]});}
            var Q17;
            {var subQ0=sQuery(id+"F0.wireOp",EDGE,"E26");var subQ1=sQuery(id+"F0.wireOp",EDGE,"E24.2.4");var subQ2=makeQuery(id+"F0.imprint","INTERSECT",VERTEX,{"derivedFrom":[subQ1,subQ0]});Q17=makeQuery(id+"F0.imprint","IMPRINT",FACE,{"disambiguationData":[TD([[makeQuery(id+"F0.imprint","IMPRINT",EDGE,{"disambiguationData":[TD([[subQ2,-1.0]])],"derivedFrom":subQ1}),-1.0]])]});}
            var Q18;
            {var subQ0=sQuery(id+"F0.wireOp",EDGE,"E26");var subQ1=sQuery(id+"F0.wireOp",EDGE,"E24.2.1");var subQ2=makeQuery(id+"F0.imprint","INTERSECT",VERTEX,{"derivedFrom":[subQ1,subQ0]});Q18=makeQuery(id+"F0.imprint","IMPRINT",FACE,{"disambiguationData":[TD([[makeQuery(id+"F0.imprint","IMPRINT",EDGE,{"disambiguationData":[TD([[subQ2,-1.0]])],"derivedFrom":subQ1}),1.0]])]});}
            var Q19;
            {var subQ0=sQuery(id+"F0.wireOp",EDGE,"E26");var subQ1=sQuery(id+"F0.wireOp",EDGE,"E24.1.4");var subQ2=makeQuery(id+"F0.imprint","INTERSECT",VERTEX,{"derivedFrom":[subQ1,subQ0]});Q19=makeQuery(id+"F0.imprint","IMPRINT",FACE,{"disambiguationData":[TD([[makeQuery(id+"F0.imprint","IMPRINT",EDGE,{"disambiguationData":[TD([[subQ2,-1.0]])],"derivedFrom":subQ1}),1.0]])]});}
            var Q20;
            {var subQ0=sQuery(id+"F0.wireOp",EDGE,"E26");var subQ1=sQuery(id+"F0.wireOp",EDGE,"E24.1.4");var subQ2=makeQuery(id+"F0.imprint","INTERSECT",VERTEX,{"derivedFrom":[subQ1,subQ0]});Q20=makeQuery(id+"F0.imprint","IMPRINT",FACE,{"disambiguationData":[TD([[makeQuery(id+"F0.imprint","IMPRINT",EDGE,{"disambiguationData":[TD([[subQ2,-1.0]])],"derivedFrom":subQ1}),-1.0]])]});}
            var Q21;
            {var subQ0=sQuery(id+"F0.wireOp",EDGE,"E19");Q21=makeQuery(id+"F0.imprint","IMPRINT",FACE,{"disambiguationData":[TD([[makeQuery(id+"F0.imprint","IMPRINT",EDGE,{"derivedFrom":subQ0}),-1.0]])]});}
            var Q22;
            {var subQ0=sQuery(id+"F0.wireOp",EDGE,"E26");var subQ1=sQuery(id+"F0.wireOp",EDGE,"E24.1.1");var subQ2=makeQuery(id+"F0.imprint","INTERSECT",VERTEX,{"derivedFrom":[subQ1,subQ0]});Q22=makeQuery(id+"F0.imprint","IMPRINT",FACE,{"disambiguationData":[TD([[makeQuery(id+"F0.imprint","IMPRINT",EDGE,{"disambiguationData":[TD([[subQ2,-1.0]])],"derivedFrom":subQ1}),1.0]])]});}
            var Q23;
            {var subQ1=sQuery(id+"F0.wireOp",EDGE,"E24.1.2");Q23=makeQuery(id+"F0.imprint","IMPRINT",FACE,{"disambiguationData":[TD([[makeQuery(id+"F0.imprint","IMPRINT",EDGE,{"derivedFrom":subQ1}),-1.0]])]});}
            var Q24;
            {var subQ1=sQuery(id+"F0.wireOp",EDGE,"E24.2.2");Q24=makeQuery(id+"F0.imprint","IMPRINT",FACE,{"disambiguationData":[TD([[makeQuery(id+"F0.imprint","IMPRINT",EDGE,{"derivedFrom":subQ1}),-1.0]])]});}
            var Q25;
            Q25 = qSketchRegion(id + "F1", true);
            extrude(context, id + "F3", {"entities" : qUnion([Q0, Q1, Q2, Q3, Q4, Q5, Q6, Q7, Q8, Q9, Q10, Q11, Q12, Q13, Q14, Q15, Q16, Q17, Q18, Q19, Q20, Q21, Q22, Q23, Q24, Q25]), "operationType" : NewBodyOperationType.ADD, "endBound" : BoundingType.SYMMETRIC, "depth" : 2.67 * mm});
        }
    });
